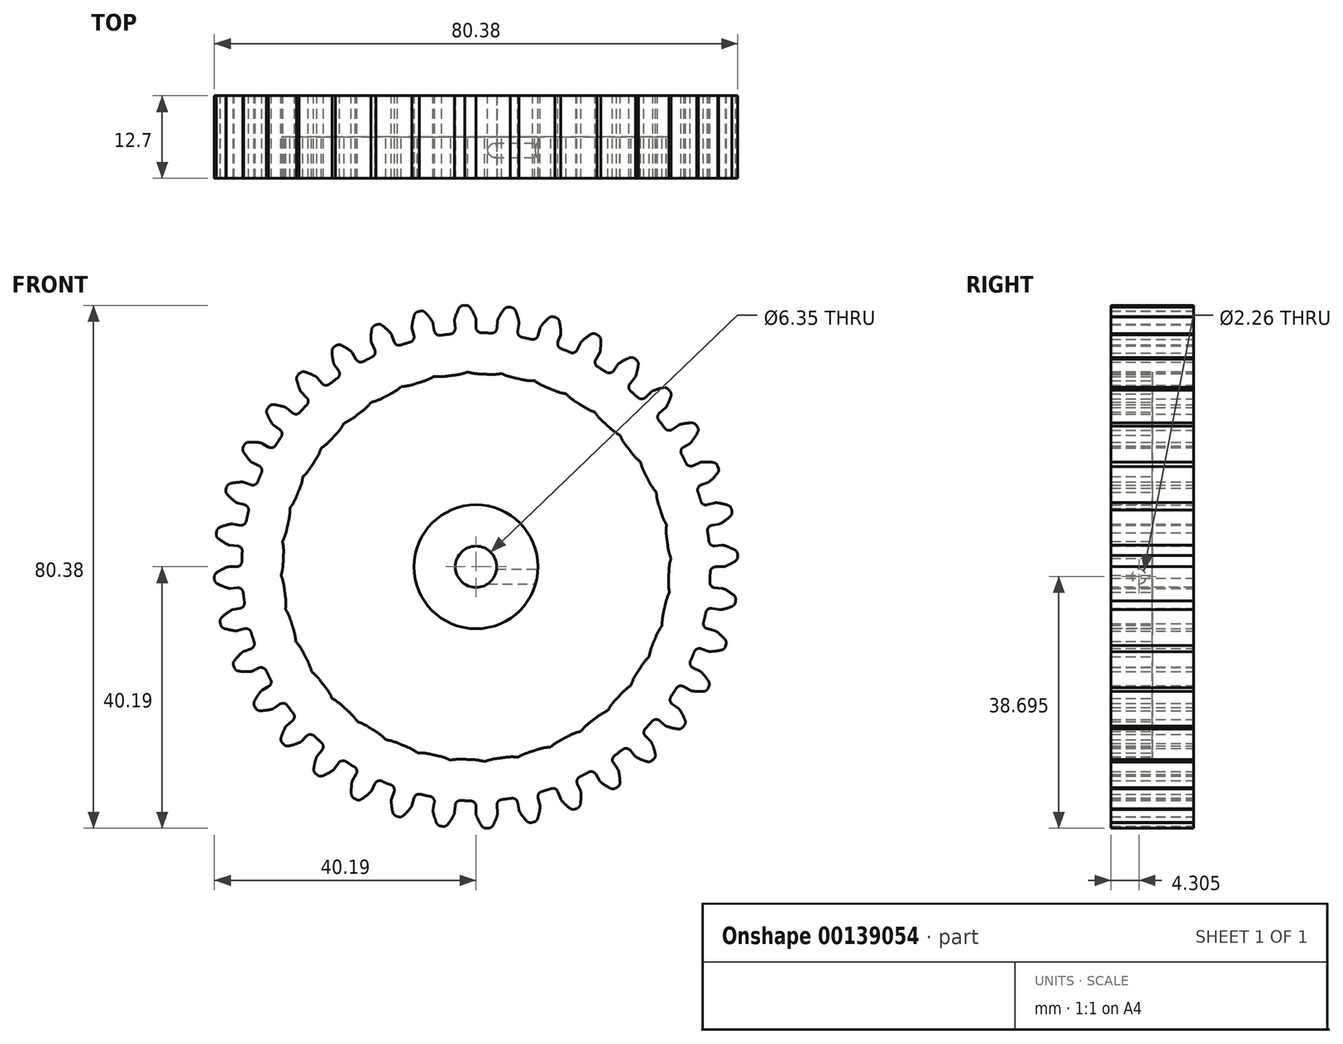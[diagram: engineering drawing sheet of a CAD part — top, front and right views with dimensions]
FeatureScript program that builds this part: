
annotation { "Feature Type Name" : "Feature", "Feature Type Description" : "" }
export const myFeature = defineFeature(function(context is Context, id is Id, definition is map)
    precondition{}
    {
        {
            var Q0;
            Q0=qCreatedBy(makeId("Front.planeOp"),FACE);
            var sketch = newSketch(context, id + "F0", { "sketchPlane" : qUnion([Q0])});
            skArc(sketch, "E0", {"start": v(-3.94, 35.77) * mm, "mid": v(-4.7, 35.68) * mm, "end": v(-5.45, 35.57) * mm});
            skArc(sketch, "E1", {"start": v(-0.06, 38.25) * mm, "mid": v(-0.43, 39.05) * mm, "end": v(-0.86, 39.8) * mm});
            skLineSegment(sketch, "E2", {"start": v(0, 37.94) * mm, "end": v(0, 36.8) * mm});
            skLineSegment(sketch, "E3", {"start": v(-1.58, 40.19) * mm, "end": v(-1.75, 40.18) * mm});
            skLineSegment(sketch, "E4.MirrorCS", {"start": v(-1.93, 40.17) * mm, "end": v(-1.75, 40.18) * mm});
            skArc(sketch, "E5.MirrorCS", {"start": v(-3.27, 38.11) * mm, "mid": v(-2.98, 38.94) * mm, "end": v(-2.61, 39.73) * mm});
            skLineSegment(sketch, "E6.MirrorCS", {"start": v(-3.3, 37.8) * mm, "end": v(-3.2, 36.66) * mm});
            skPoint(sketch, "E7.visualSharp", {"position": v(-3.32, 37.96) * mm});
            skArc(sketch, "E7.filletArc", {"start": v(-3.27, 38.11) * mm, "mid": v(-3.3, 37.96) * mm, "end": v(-3.3, 37.8) * mm});
            skPoint(sketch, "E8.visualSharp", {"position": v(0, 38.1) * mm});
            skArc(sketch, "E8.filletArc", {"start": v(0, 37.94) * mm, "mid": v(-0.02, 38.1) * mm, "end": v(-0.06, 38.25) * mm});
            skPoint(sketch, "E9.visualSharp", {"position": v(-2.38, 40.15) * mm});
            skArc(sketch, "E9.filletArc", {"start": v(-1.93, 40.17) * mm, "mid": v(-2.33, 40.04) * mm, "end": v(-2.61, 39.73) * mm});
            skPoint(sketch, "E10.visualSharp", {"position": v(-1.13, 40.2) * mm});
            skArc(sketch, "E10.filletArc", {"start": v(-0.86, 39.8) * mm, "mid": v(-1.17, 40.1) * mm, "end": v(-1.58, 40.19) * mm});
            skPoint(sketch, "E11.visualSharp", {"position": v(-3.14, 35.85) * mm});
            skArc(sketch, "E11.filletArc", {"start": v(-3.94, 35.77) * mm, "mid": v(-3.4, 36.06) * mm, "end": v(-3.2, 36.66) * mm});
            skPoint(sketch, "E12.visualSharp", {"position": v(0, 35.98) * mm});
            skArc(sketch, "E12.filletArc", {"start": v(0, 36.8) * mm, "mid": v(0.24, 36.22) * mm, "end": v(0.8, 35.97) * mm});
            skArc(sketch, "E13.1.0", {"start": v(-10.1, 34.54) * mm, "mid": v(-9.6, 34.93) * mm, "end": v(-9.52, 35.55) * mm});
            skLineSegment(sketch, "E13.1.1", {"start": v(-9.82, 36.65) * mm, "end": v(-9.52, 35.55) * mm});
            skArc(sketch, "E13.1.2", {"start": v(-9.84, 36.96) * mm, "mid": v(-9.85, 36.8) * mm, "end": v(-9.82, 36.65) * mm});
            skArc(sketch, "E13.1.3", {"start": v(-9.84, 36.96) * mm, "mid": v(-9.7, 37.83) * mm, "end": v(-9.47, 38.67) * mm});
            skArc(sketch, "E13.1.4", {"start": v(-8.87, 39.23) * mm, "mid": v(-9.25, 39.03) * mm, "end": v(-9.47, 38.67) * mm});
            skLineSegment(sketch, "E13.1.5", {"start": v(-8.87, 39.23) * mm, "end": v(-8.7, 39.27) * mm});
            skLineSegment(sketch, "E13.1.6", {"start": v(-8.54, 39.3) * mm, "end": v(-8.7, 39.27) * mm});
            skArc(sketch, "E13.1.7", {"start": v(-7.76, 39.05) * mm, "mid": v(-8.12, 39.28) * mm, "end": v(-8.54, 39.3) * mm});
            skArc(sketch, "E13.1.8", {"start": v(-6.7, 37.66) * mm, "mid": v(-7.2, 38.38) * mm, "end": v(-7.76, 39.05) * mm});
            skArc(sketch, "E13.1.9", {"start": v(-6.59, 37.37) * mm, "mid": v(-6.63, 37.52) * mm, "end": v(-6.7, 37.66) * mm});
            skArc(sketch, "E13.1.10", {"start": v(-6.4, 36.24) * mm, "mid": v(-6.06, 35.71) * mm, "end": v(-5.45, 35.57) * mm});
            skLineSegment(sketch, "E13.1.11", {"start": v(-6.59, 37.37) * mm, "end": v(-6.4, 36.24) * mm});
            skArc(sketch, "E13.2.0", {"start": v(-15.93, 32.26) * mm, "mid": v(-15.52, 32.73) * mm, "end": v(-15.55, 33.35) * mm});
            skLineSegment(sketch, "E13.2.1", {"start": v(-16.04, 34.39) * mm, "end": v(-15.55, 33.35) * mm});
            skArc(sketch, "E13.2.2", {"start": v(-16.11, 34.7) * mm, "mid": v(-16.09, 34.54) * mm, "end": v(-16.04, 34.39) * mm});
            skArc(sketch, "E13.2.3", {"start": v(-16.11, 34.7) * mm, "mid": v(-16.12, 35.57) * mm, "end": v(-16.04, 36.44) * mm});
            skArc(sketch, "E13.2.4", {"start": v(-15.55, 37.1) * mm, "mid": v(-15.88, 36.83) * mm, "end": v(-16.04, 36.44) * mm});
            skLineSegment(sketch, "E13.2.5", {"start": v(-15.55, 37.1) * mm, "end": v(-15.4, 37.16) * mm});
            skLineSegment(sketch, "E13.2.6", {"start": v(-15.23, 37.22) * mm, "end": v(-15.4, 37.16) * mm});
            skArc(sketch, "E13.2.7", {"start": v(-14.43, 37.11) * mm, "mid": v(-14.81, 37.27) * mm, "end": v(-15.23, 37.22) * mm});
            skArc(sketch, "E13.2.8", {"start": v(-13.14, 35.93) * mm, "mid": v(-13.76, 36.55) * mm, "end": v(-14.43, 37.11) * mm});
            skArc(sketch, "E13.2.9", {"start": v(-12.98, 35.65) * mm, "mid": v(-13.05, 35.8) * mm, "end": v(-13.14, 35.93) * mm});
            skArc(sketch, "E13.2.10", {"start": v(-12.59, 34.58) * mm, "mid": v(-12.17, 34.12) * mm, "end": v(-11.55, 34.08) * mm});
            skLineSegment(sketch, "E13.2.11", {"start": v(-12.98, 35.65) * mm, "end": v(-12.59, 34.58) * mm});
            skArc(sketch, "E13.3.0", {"start": v(-21.3, 29) * mm, "mid": v(-20.97, 29.54) * mm, "end": v(-21.1, 30.14) * mm});
            skLineSegment(sketch, "E13.3.1", {"start": v(-21.76, 31.08) * mm, "end": v(-21.1, 30.14) * mm});
            skArc(sketch, "E13.3.2", {"start": v(-21.9, 31.37) * mm, "mid": v(-21.84, 31.22) * mm, "end": v(-21.76, 31.08) * mm});
            skArc(sketch, "E13.3.3", {"start": v(-21.9, 31.37) * mm, "mid": v(-22.05, 32.23) * mm, "end": v(-22.13, 33.1) * mm});
            skArc(sketch, "E13.3.4", {"start": v(-21.76, 33.83) * mm, "mid": v(-22.04, 33.51) * mm, "end": v(-22.13, 33.1) * mm});
            skLineSegment(sketch, "E13.3.5", {"start": v(-21.76, 33.83) * mm, "end": v(-21.61, 33.92) * mm});
            skLineSegment(sketch, "E13.3.6", {"start": v(-21.46, 34.01) * mm, "end": v(-21.61, 33.92) * mm});
            skArc(sketch, "E13.3.7", {"start": v(-20.65, 34.04) * mm, "mid": v(-21.06, 34.14) * mm, "end": v(-21.46, 34.01) * mm});
            skArc(sketch, "E13.3.8", {"start": v(-19.18, 33.1) * mm, "mid": v(-19.9, 33.6) * mm, "end": v(-20.65, 34.04) * mm});
            skArc(sketch, "E13.3.9", {"start": v(-18.97, 32.86) * mm, "mid": v(-19.06, 32.99) * mm, "end": v(-19.18, 33.1) * mm});
            skArc(sketch, "E13.3.10", {"start": v(-18.4, 31.87) * mm, "mid": v(-17.9, 31.49) * mm, "end": v(-17.29, 31.56) * mm});
            skLineSegment(sketch, "E13.3.11", {"start": v(-18.97, 32.86) * mm, "end": v(-18.4, 31.87) * mm});
            skArc(sketch, "E13.4.0", {"start": v(-26, 24.87) * mm, "mid": v(-25.78, 25.45) * mm, "end": v(-26.02, 26.02) * mm});
            skLineSegment(sketch, "E13.4.1", {"start": v(-26.83, 26.83) * mm, "end": v(-26.02, 26.02) * mm});
            skArc(sketch, "E13.4.2", {"start": v(-27, 27.1) * mm, "mid": v(-26.93, 26.95) * mm, "end": v(-26.83, 26.83) * mm});
            skArc(sketch, "E13.4.3", {"start": v(-27, 27.1) * mm, "mid": v(-27.31, 27.91) * mm, "end": v(-27.54, 28.76) * mm});
            skArc(sketch, "E13.4.4", {"start": v(-27.3, 29.54) * mm, "mid": v(-27.52, 29.18) * mm, "end": v(-27.54, 28.76) * mm});
            skLineSegment(sketch, "E13.4.5", {"start": v(-27.3, 29.54) * mm, "end": v(-27.17, 29.65) * mm});
            skLineSegment(sketch, "E13.4.6", {"start": v(-27.04, 29.77) * mm, "end": v(-27.17, 29.65) * mm});
            skArc(sketch, "E13.4.7", {"start": v(-26.25, 29.94) * mm, "mid": v(-26.67, 29.96) * mm, "end": v(-27.04, 29.77) * mm});
            skArc(sketch, "E13.4.8", {"start": v(-24.63, 29.26) * mm, "mid": v(-25.43, 29.64) * mm, "end": v(-26.25, 29.94) * mm});
            skArc(sketch, "E13.4.9", {"start": v(-24.39, 29.07) * mm, "mid": v(-24.5, 29.18) * mm, "end": v(-24.63, 29.26) * mm});
            skArc(sketch, "E13.4.10", {"start": v(-23.65, 28.2) * mm, "mid": v(-23.1, 27.9) * mm, "end": v(-22.5, 28.08) * mm});
            skLineSegment(sketch, "E13.4.11", {"start": v(-24.39, 29.07) * mm, "end": v(-23.65, 28.2) * mm});
            skArc(sketch, "E13.5.0", {"start": v(-29.93, 19.97) * mm, "mid": v(-29.8, 20.58) * mm, "end": v(-30.14, 21.1) * mm});
            skLineSegment(sketch, "E13.5.1", {"start": v(-31.08, 21.76) * mm, "end": v(-30.14, 21.1) * mm});
            skArc(sketch, "E13.5.2", {"start": v(-31.3, 22) * mm, "mid": v(-31.2, 21.87) * mm, "end": v(-31.08, 21.76) * mm});
            skArc(sketch, "E13.5.3", {"start": v(-31.3, 22) * mm, "mid": v(-31.74, 22.75) * mm, "end": v(-32.11, 23.54) * mm});
            skArc(sketch, "E13.5.4", {"start": v(-32.01, 24.35) * mm, "mid": v(-32.17, 23.96) * mm, "end": v(-32.11, 23.54) * mm});
            skLineSegment(sketch, "E13.5.5", {"start": v(-32.01, 24.35) * mm, "end": v(-31.9, 24.49) * mm});
            skLineSegment(sketch, "E13.5.6", {"start": v(-31.8, 24.62) * mm, "end": v(-31.9, 24.49) * mm});
            skArc(sketch, "E13.5.7", {"start": v(-31.05, 24.93) * mm, "mid": v(-31.47, 24.87) * mm, "end": v(-31.8, 24.62) * mm});
            skArc(sketch, "E13.5.8", {"start": v(-29.34, 24.54) * mm, "mid": v(-30.19, 24.77) * mm, "end": v(-31.05, 24.93) * mm});
            skArc(sketch, "E13.5.9", {"start": v(-29.07, 24.39) * mm, "mid": v(-29.2, 24.48) * mm, "end": v(-29.34, 24.54) * mm});
            skArc(sketch, "E13.5.10", {"start": v(-28.2, 23.65) * mm, "mid": v(-27.6, 23.46) * mm, "end": v(-27.04, 23.74) * mm});
            skLineSegment(sketch, "E13.5.11", {"start": v(-29.07, 24.39) * mm, "end": v(-28.2, 23.65) * mm});
            skArc(sketch, "E13.6.0", {"start": v(-32.94, 14.47) * mm, "mid": v(-32.93, 15.1) * mm, "end": v(-33.35, 15.55) * mm});
            skLineSegment(sketch, "E13.6.1", {"start": v(-34.39, 16.04) * mm, "end": v(-33.35, 15.55) * mm});
            skArc(sketch, "E13.6.2", {"start": v(-34.64, 16.22) * mm, "mid": v(-34.52, 16.12) * mm, "end": v(-34.39, 16.04) * mm});
            skArc(sketch, "E13.6.3", {"start": v(-34.64, 16.22) * mm, "mid": v(-35.21, 16.89) * mm, "end": v(-35.71, 17.6) * mm});
            skArc(sketch, "E13.6.4", {"start": v(-35.75, 18.42) * mm, "mid": v(-35.84, 18) * mm, "end": v(-35.71, 17.6) * mm});
            skLineSegment(sketch, "E13.6.5", {"start": v(-35.75, 18.42) * mm, "end": v(-35.68, 18.57) * mm});
            skLineSegment(sketch, "E13.6.6", {"start": v(-35.6, 18.72) * mm, "end": v(-35.68, 18.57) * mm});
            skArc(sketch, "E13.6.7", {"start": v(-34.9, 19.16) * mm, "mid": v(-35.3, 19.03) * mm, "end": v(-35.6, 18.72) * mm});
            skArc(sketch, "E13.6.8", {"start": v(-33.16, 19.07) * mm, "mid": v(-34.03, 19.16) * mm, "end": v(-34.9, 19.16) * mm});
            skArc(sketch, "E13.6.9", {"start": v(-32.86, 18.97) * mm, "mid": v(-33, 19.04) * mm, "end": v(-33.16, 19.07) * mm});
            skArc(sketch, "E13.6.10", {"start": v(-31.87, 18.4) * mm, "mid": v(-31.25, 18.31) * mm, "end": v(-30.75, 18.69) * mm});
            skLineSegment(sketch, "E13.6.11", {"start": v(-32.86, 18.97) * mm, "end": v(-31.87, 18.4) * mm});
            skArc(sketch, "E13.7.0", {"start": v(-34.96, 8.53) * mm, "mid": v(-35.05, 9.15) * mm, "end": v(-35.55, 9.52) * mm});
            skLineSegment(sketch, "E13.7.1", {"start": v(-36.65, 9.82) * mm, "end": v(-35.55, 9.52) * mm});
            skArc(sketch, "E13.7.2", {"start": v(-36.93, 9.96) * mm, "mid": v(-36.8, 9.88) * mm, "end": v(-36.65, 9.82) * mm});
            skArc(sketch, "E13.7.3", {"start": v(-36.93, 9.96) * mm, "mid": v(-37.6, 10.52) * mm, "end": v(-38.23, 11.14) * mm});
            skArc(sketch, "E13.7.4", {"start": v(-38.4, 11.93) * mm, "mid": v(-38.42, 11.5) * mm, "end": v(-38.23, 11.14) * mm});
            skLineSegment(sketch, "E13.7.5", {"start": v(-38.4, 11.93) * mm, "end": v(-38.36, 12.1) * mm});
            skLineSegment(sketch, "E13.7.6", {"start": v(-38.3, 12.26) * mm, "end": v(-38.36, 12.1) * mm});
            skArc(sketch, "E13.7.7", {"start": v(-37.7, 12.8) * mm, "mid": v(-38.08, 12.61) * mm, "end": v(-38.3, 12.26) * mm});
            skArc(sketch, "E13.7.8", {"start": v(-35.97, 13.03) * mm, "mid": v(-36.84, 12.96) * mm, "end": v(-37.7, 12.8) * mm});
            skArc(sketch, "E13.7.9", {"start": v(-35.65, 12.98) * mm, "mid": v(-35.8, 13.02) * mm, "end": v(-35.97, 13.03) * mm});
            skArc(sketch, "E13.7.10", {"start": v(-34.58, 12.59) * mm, "mid": v(-33.96, 12.6) * mm, "end": v(-33.53, 13.06) * mm});
            skLineSegment(sketch, "E13.7.11", {"start": v(-35.65, 12.98) * mm, "end": v(-34.58, 12.59) * mm});
            skArc(sketch, "E13.8.0", {"start": v(-35.9, 2.33) * mm, "mid": v(-36.1, 2.92) * mm, "end": v(-36.66, 3.2) * mm});
            skLineSegment(sketch, "E13.8.1", {"start": v(-37.8, 3.3) * mm, "end": v(-36.66, 3.2) * mm});
            skArc(sketch, "E13.8.2", {"start": v(-38.1, 3.4) * mm, "mid": v(-37.95, 3.34) * mm, "end": v(-37.8, 3.3) * mm});
            skArc(sketch, "E13.8.3", {"start": v(-38.1, 3.4) * mm, "mid": v(-38.86, 3.83) * mm, "end": v(-39.58, 4.33) * mm});
            skArc(sketch, "E13.8.4", {"start": v(-39.9, 5.08) * mm, "mid": v(-39.84, 4.66) * mm, "end": v(-39.58, 4.33) * mm});
            skLineSegment(sketch, "E13.8.5", {"start": v(-39.9, 5.08) * mm, "end": v(-39.88, 5.25) * mm});
            skLineSegment(sketch, "E13.8.6", {"start": v(-39.85, 5.42) * mm, "end": v(-39.88, 5.25) * mm});
            skArc(sketch, "E13.8.7", {"start": v(-39.35, 6.06) * mm, "mid": v(-39.69, 5.8) * mm, "end": v(-39.85, 5.42) * mm});
            skArc(sketch, "E13.8.8", {"start": v(-37.68, 6.58) * mm, "mid": v(-38.53, 6.36) * mm, "end": v(-39.35, 6.06) * mm});
            skArc(sketch, "E13.8.9", {"start": v(-37.37, 6.59) * mm, "mid": v(-37.52, 6.6) * mm, "end": v(-37.68, 6.58) * mm});
            skArc(sketch, "E13.8.10", {"start": v(-36.24, 6.4) * mm, "mid": v(-35.63, 6.52) * mm, "end": v(-35.29, 7.04) * mm});
            skLineSegment(sketch, "E13.8.11", {"start": v(-37.37, 6.59) * mm, "end": v(-36.24, 6.4) * mm});
            skArc(sketch, "E13.9.0", {"start": v(-35.77, -3.94) * mm, "mid": v(-36.06, -3.4) * mm, "end": v(-36.66, -3.2) * mm});
            skLineSegment(sketch, "E13.9.1", {"start": v(-37.8, -3.3) * mm, "end": v(-36.66, -3.2) * mm});
            skArc(sketch, "E13.9.2", {"start": v(-38.11, -3.27) * mm, "mid": v(-37.96, -3.3) * mm, "end": v(-37.8, -3.3) * mm});
            skArc(sketch, "E13.9.3", {"start": v(-38.11, -3.27) * mm, "mid": v(-38.94, -2.98) * mm, "end": v(-39.73, -2.61) * mm});
            skArc(sketch, "E13.9.4", {"start": v(-40.17, -1.93) * mm, "mid": v(-40.04, -2.33) * mm, "end": v(-39.73, -2.61) * mm});
            skLineSegment(sketch, "E13.9.5", {"start": v(-40.17, -1.93) * mm, "end": v(-40.18, -1.75) * mm});
            skLineSegment(sketch, "E13.9.6", {"start": v(-40.19, -1.58) * mm, "end": v(-40.18, -1.75) * mm});
            skArc(sketch, "E13.9.7", {"start": v(-39.8, -0.86) * mm, "mid": v(-40.1, -1.17) * mm, "end": v(-40.19, -1.58) * mm});
            skArc(sketch, "E13.9.8", {"start": v(-38.25, -0.06) * mm, "mid": v(-39.05, -0.43) * mm, "end": v(-39.8, -0.86) * mm});
            skArc(sketch, "E13.9.9", {"start": v(-37.94, 0) * mm, "mid": v(-38.1, -0.02) * mm, "end": v(-38.25, -0.06) * mm});
            skArc(sketch, "E13.9.10", {"start": v(-36.8, 0) * mm, "mid": v(-36.22, 0.24) * mm, "end": v(-35.97, 0.8) * mm});
            skLineSegment(sketch, "E13.9.11", {"start": v(-37.94, 0) * mm, "end": v(-36.8, 0) * mm});
            skArc(sketch, "E13.10.0", {"start": v(-34.54, -10.1) * mm, "mid": v(-34.93, -9.6) * mm, "end": v(-35.55, -9.52) * mm});
            skLineSegment(sketch, "E13.10.1", {"start": v(-36.65, -9.82) * mm, "end": v(-35.55, -9.52) * mm});
            skArc(sketch, "E13.10.2", {"start": v(-36.96, -9.84) * mm, "mid": v(-36.8, -9.85) * mm, "end": v(-36.65, -9.82) * mm});
            skArc(sketch, "E13.10.3", {"start": v(-36.96, -9.84) * mm, "mid": v(-37.83, -9.7) * mm, "end": v(-38.67, -9.47) * mm});
            skArc(sketch, "E13.10.4", {"start": v(-39.23, -8.87) * mm, "mid": v(-39.03, -9.25) * mm, "end": v(-38.67, -9.47) * mm});
            skLineSegment(sketch, "E13.10.5", {"start": v(-39.23, -8.87) * mm, "end": v(-39.27, -8.7) * mm});
            skLineSegment(sketch, "E13.10.6", {"start": v(-39.3, -8.54) * mm, "end": v(-39.27, -8.7) * mm});
            skArc(sketch, "E13.10.7", {"start": v(-39.05, -7.76) * mm, "mid": v(-39.28, -8.12) * mm, "end": v(-39.3, -8.54) * mm});
            skArc(sketch, "E13.10.8", {"start": v(-37.66, -6.7) * mm, "mid": v(-38.38, -7.2) * mm, "end": v(-39.05, -7.76) * mm});
            skArc(sketch, "E13.10.9", {"start": v(-37.37, -6.59) * mm, "mid": v(-37.52, -6.63) * mm, "end": v(-37.66, -6.7) * mm});
            skArc(sketch, "E13.10.10", {"start": v(-36.24, -6.4) * mm, "mid": v(-35.71, -6.06) * mm, "end": v(-35.57, -5.45) * mm});
            skLineSegment(sketch, "E13.10.11", {"start": v(-37.37, -6.59) * mm, "end": v(-36.24, -6.4) * mm});
            skArc(sketch, "E13.11.0", {"start": v(-32.26, -15.93) * mm, "mid": v(-32.73, -15.52) * mm, "end": v(-33.35, -15.55) * mm});
            skLineSegment(sketch, "E13.11.1", {"start": v(-34.39, -16.04) * mm, "end": v(-33.35, -15.55) * mm});
            skArc(sketch, "E13.11.2", {"start": v(-34.7, -16.11) * mm, "mid": v(-34.54, -16.09) * mm, "end": v(-34.39, -16.04) * mm});
            skArc(sketch, "E13.11.3", {"start": v(-34.7, -16.11) * mm, "mid": v(-35.57, -16.12) * mm, "end": v(-36.44, -16.04) * mm});
            skArc(sketch, "E13.11.4", {"start": v(-37.1, -15.55) * mm, "mid": v(-36.83, -15.88) * mm, "end": v(-36.44, -16.04) * mm});
            skLineSegment(sketch, "E13.11.5", {"start": v(-37.1, -15.55) * mm, "end": v(-37.16, -15.4) * mm});
            skLineSegment(sketch, "E13.11.6", {"start": v(-37.22, -15.23) * mm, "end": v(-37.16, -15.4) * mm});
            skArc(sketch, "E13.11.7", {"start": v(-37.11, -14.43) * mm, "mid": v(-37.27, -14.81) * mm, "end": v(-37.22, -15.23) * mm});
            skArc(sketch, "E13.11.8", {"start": v(-35.93, -13.14) * mm, "mid": v(-36.55, -13.76) * mm, "end": v(-37.11, -14.43) * mm});
            skArc(sketch, "E13.11.9", {"start": v(-35.65, -12.98) * mm, "mid": v(-35.8, -13.05) * mm, "end": v(-35.93, -13.14) * mm});
            skArc(sketch, "E13.11.10", {"start": v(-34.58, -12.59) * mm, "mid": v(-34.12, -12.17) * mm, "end": v(-34.08, -11.55) * mm});
            skLineSegment(sketch, "E13.11.11", {"start": v(-35.65, -12.98) * mm, "end": v(-34.58, -12.59) * mm});
            skArc(sketch, "E13.12.0", {"start": v(-29, -21.3) * mm, "mid": v(-29.54, -20.97) * mm, "end": v(-30.14, -21.1) * mm});
            skLineSegment(sketch, "E13.12.1", {"start": v(-31.08, -21.76) * mm, "end": v(-30.14, -21.1) * mm});
            skArc(sketch, "E13.12.2", {"start": v(-31.37, -21.9) * mm, "mid": v(-31.22, -21.84) * mm, "end": v(-31.08, -21.76) * mm});
            skArc(sketch, "E13.12.3", {"start": v(-31.37, -21.9) * mm, "mid": v(-32.23, -22.05) * mm, "end": v(-33.1, -22.13) * mm});
            skArc(sketch, "E13.12.4", {"start": v(-33.83, -21.76) * mm, "mid": v(-33.51, -22.04) * mm, "end": v(-33.1, -22.13) * mm});
            skLineSegment(sketch, "E13.12.5", {"start": v(-33.83, -21.76) * mm, "end": v(-33.92, -21.61) * mm});
            skLineSegment(sketch, "E13.12.6", {"start": v(-34.01, -21.46) * mm, "end": v(-33.92, -21.61) * mm});
            skArc(sketch, "E13.12.7", {"start": v(-34.04, -20.65) * mm, "mid": v(-34.14, -21.06) * mm, "end": v(-34.01, -21.46) * mm});
            skArc(sketch, "E13.12.8", {"start": v(-33.1, -19.18) * mm, "mid": v(-33.6, -19.9) * mm, "end": v(-34.04, -20.65) * mm});
            skArc(sketch, "E13.12.9", {"start": v(-32.86, -18.97) * mm, "mid": v(-32.99, -19.06) * mm, "end": v(-33.1, -19.18) * mm});
            skArc(sketch, "E13.12.10", {"start": v(-31.87, -18.4) * mm, "mid": v(-31.49, -17.9) * mm, "end": v(-31.56, -17.29) * mm});
            skLineSegment(sketch, "E13.12.11", {"start": v(-32.86, -18.97) * mm, "end": v(-31.87, -18.4) * mm});
            skArc(sketch, "E13.13.0", {"start": v(-24.87, -26) * mm, "mid": v(-25.45, -25.78) * mm, "end": v(-26.02, -26.02) * mm});
            skLineSegment(sketch, "E13.13.1", {"start": v(-26.83, -26.83) * mm, "end": v(-26.02, -26.02) * mm});
            skArc(sketch, "E13.13.2", {"start": v(-27.1, -27) * mm, "mid": v(-26.95, -26.93) * mm, "end": v(-26.83, -26.83) * mm});
            skArc(sketch, "E13.13.3", {"start": v(-27.1, -27) * mm, "mid": v(-27.91, -27.31) * mm, "end": v(-28.76, -27.54) * mm});
            skArc(sketch, "E13.13.4", {"start": v(-29.54, -27.3) * mm, "mid": v(-29.18, -27.52) * mm, "end": v(-28.76, -27.54) * mm});
            skLineSegment(sketch, "E13.13.5", {"start": v(-29.54, -27.3) * mm, "end": v(-29.65, -27.17) * mm});
            skLineSegment(sketch, "E13.13.6", {"start": v(-29.77, -27.04) * mm, "end": v(-29.65, -27.17) * mm});
            skArc(sketch, "E13.13.7", {"start": v(-29.94, -26.25) * mm, "mid": v(-29.96, -26.67) * mm, "end": v(-29.77, -27.04) * mm});
            skArc(sketch, "E13.13.8", {"start": v(-29.26, -24.63) * mm, "mid": v(-29.64, -25.43) * mm, "end": v(-29.94, -26.25) * mm});
            skArc(sketch, "E13.13.9", {"start": v(-29.07, -24.39) * mm, "mid": v(-29.18, -24.5) * mm, "end": v(-29.26, -24.63) * mm});
            skArc(sketch, "E13.13.10", {"start": v(-28.2, -23.65) * mm, "mid": v(-27.9, -23.1) * mm, "end": v(-28.08, -22.5) * mm});
            skLineSegment(sketch, "E13.13.11", {"start": v(-29.07, -24.39) * mm, "end": v(-28.2, -23.65) * mm});
            skArc(sketch, "E13.14.0", {"start": v(-19.97, -29.93) * mm, "mid": v(-20.58, -29.8) * mm, "end": v(-21.1, -30.14) * mm});
            skLineSegment(sketch, "E13.14.1", {"start": v(-21.76, -31.08) * mm, "end": v(-21.1, -30.14) * mm});
            skArc(sketch, "E13.14.2", {"start": v(-22, -31.3) * mm, "mid": v(-21.87, -31.2) * mm, "end": v(-21.76, -31.08) * mm});
            skArc(sketch, "E13.14.3", {"start": v(-22, -31.3) * mm, "mid": v(-22.75, -31.74) * mm, "end": v(-23.54, -32.11) * mm});
            skArc(sketch, "E13.14.4", {"start": v(-24.35, -32.01) * mm, "mid": v(-23.96, -32.17) * mm, "end": v(-23.54, -32.11) * mm});
            skLineSegment(sketch, "E13.14.5", {"start": v(-24.35, -32.01) * mm, "end": v(-24.49, -31.9) * mm});
            skLineSegment(sketch, "E13.14.6", {"start": v(-24.62, -31.8) * mm, "end": v(-24.49, -31.9) * mm});
            skArc(sketch, "E13.14.7", {"start": v(-24.93, -31.05) * mm, "mid": v(-24.87, -31.47) * mm, "end": v(-24.62, -31.8) * mm});
            skArc(sketch, "E13.14.8", {"start": v(-24.54, -29.34) * mm, "mid": v(-24.77, -30.19) * mm, "end": v(-24.93, -31.05) * mm});
            skArc(sketch, "E13.14.9", {"start": v(-24.39, -29.07) * mm, "mid": v(-24.48, -29.2) * mm, "end": v(-24.54, -29.34) * mm});
            skArc(sketch, "E13.14.10", {"start": v(-23.65, -28.2) * mm, "mid": v(-23.46, -27.6) * mm, "end": v(-23.74, -27.04) * mm});
            skLineSegment(sketch, "E13.14.11", {"start": v(-24.39, -29.07) * mm, "end": v(-23.65, -28.2) * mm});
            skArc(sketch, "E13.15.0", {"start": v(-14.47, -32.94) * mm, "mid": v(-15.1, -32.93) * mm, "end": v(-15.55, -33.35) * mm});
            skLineSegment(sketch, "E13.15.1", {"start": v(-16.04, -34.39) * mm, "end": v(-15.55, -33.35) * mm});
            skArc(sketch, "E13.15.2", {"start": v(-16.22, -34.64) * mm, "mid": v(-16.12, -34.52) * mm, "end": v(-16.04, -34.39) * mm});
            skArc(sketch, "E13.15.3", {"start": v(-16.22, -34.64) * mm, "mid": v(-16.89, -35.21) * mm, "end": v(-17.6, -35.71) * mm});
            skArc(sketch, "E13.15.4", {"start": v(-18.42, -35.75) * mm, "mid": v(-18, -35.84) * mm, "end": v(-17.6, -35.71) * mm});
            skLineSegment(sketch, "E13.15.5", {"start": v(-18.42, -35.75) * mm, "end": v(-18.57, -35.68) * mm});
            skLineSegment(sketch, "E13.15.6", {"start": v(-18.72, -35.6) * mm, "end": v(-18.57, -35.68) * mm});
            skArc(sketch, "E13.15.7", {"start": v(-19.16, -34.9) * mm, "mid": v(-19.03, -35.3) * mm, "end": v(-18.72, -35.6) * mm});
            skArc(sketch, "E13.15.8", {"start": v(-19.07, -33.16) * mm, "mid": v(-19.16, -34.03) * mm, "end": v(-19.16, -34.9) * mm});
            skArc(sketch, "E13.15.9", {"start": v(-18.97, -32.86) * mm, "mid": v(-19.04, -33) * mm, "end": v(-19.07, -33.16) * mm});
            skArc(sketch, "E13.15.10", {"start": v(-18.4, -31.87) * mm, "mid": v(-18.31, -31.25) * mm, "end": v(-18.69, -30.75) * mm});
            skLineSegment(sketch, "E13.15.11", {"start": v(-18.97, -32.86) * mm, "end": v(-18.4, -31.87) * mm});
            skArc(sketch, "E13.16.0", {"start": v(-8.53, -34.96) * mm, "mid": v(-9.15, -35.05) * mm, "end": v(-9.52, -35.55) * mm});
            skLineSegment(sketch, "E13.16.1", {"start": v(-9.82, -36.65) * mm, "end": v(-9.52, -35.55) * mm});
            skArc(sketch, "E13.16.2", {"start": v(-9.96, -36.93) * mm, "mid": v(-9.88, -36.8) * mm, "end": v(-9.82, -36.65) * mm});
            skArc(sketch, "E13.16.3", {"start": v(-9.96, -36.93) * mm, "mid": v(-10.52, -37.6) * mm, "end": v(-11.14, -38.23) * mm});
            skArc(sketch, "E13.16.4", {"start": v(-11.93, -38.4) * mm, "mid": v(-11.5, -38.42) * mm, "end": v(-11.14, -38.23) * mm});
            skLineSegment(sketch, "E13.16.5", {"start": v(-11.93, -38.4) * mm, "end": v(-12.1, -38.36) * mm});
            skLineSegment(sketch, "E13.16.6", {"start": v(-12.26, -38.3) * mm, "end": v(-12.1, -38.36) * mm});
            skArc(sketch, "E13.16.7", {"start": v(-12.8, -37.7) * mm, "mid": v(-12.61, -38.08) * mm, "end": v(-12.26, -38.3) * mm});
            skArc(sketch, "E13.16.8", {"start": v(-13.03, -35.97) * mm, "mid": v(-12.96, -36.84) * mm, "end": v(-12.8, -37.7) * mm});
            skArc(sketch, "E13.16.9", {"start": v(-12.98, -35.65) * mm, "mid": v(-13.02, -35.8) * mm, "end": v(-13.03, -35.97) * mm});
            skArc(sketch, "E13.16.10", {"start": v(-12.59, -34.58) * mm, "mid": v(-12.6, -33.96) * mm, "end": v(-13.06, -33.53) * mm});
            skLineSegment(sketch, "E13.16.11", {"start": v(-12.98, -35.65) * mm, "end": v(-12.59, -34.58) * mm});
            skArc(sketch, "E13.17.0", {"start": v(-2.33, -35.9) * mm, "mid": v(-2.92, -36.1) * mm, "end": v(-3.2, -36.66) * mm});
            skLineSegment(sketch, "E13.17.1", {"start": v(-3.3, -37.8) * mm, "end": v(-3.2, -36.66) * mm});
            skArc(sketch, "E13.17.2", {"start": v(-3.4, -38.1) * mm, "mid": v(-3.34, -37.95) * mm, "end": v(-3.3, -37.8) * mm});
            skArc(sketch, "E13.17.3", {"start": v(-3.4, -38.1) * mm, "mid": v(-3.83, -38.86) * mm, "end": v(-4.33, -39.58) * mm});
            skArc(sketch, "E13.17.4", {"start": v(-5.08, -39.9) * mm, "mid": v(-4.66, -39.84) * mm, "end": v(-4.33, -39.58) * mm});
            skLineSegment(sketch, "E13.17.5", {"start": v(-5.08, -39.9) * mm, "end": v(-5.25, -39.88) * mm});
            skLineSegment(sketch, "E13.17.6", {"start": v(-5.42, -39.85) * mm, "end": v(-5.25, -39.88) * mm});
            skArc(sketch, "E13.17.7", {"start": v(-6.06, -39.35) * mm, "mid": v(-5.8, -39.69) * mm, "end": v(-5.42, -39.85) * mm});
            skArc(sketch, "E13.17.8", {"start": v(-6.58, -37.68) * mm, "mid": v(-6.36, -38.53) * mm, "end": v(-6.06, -39.35) * mm});
            skArc(sketch, "E13.17.9", {"start": v(-6.59, -37.37) * mm, "mid": v(-6.6, -37.52) * mm, "end": v(-6.58, -37.68) * mm});
            skArc(sketch, "E13.17.10", {"start": v(-6.4, -36.24) * mm, "mid": v(-6.52, -35.63) * mm, "end": v(-7.04, -35.29) * mm});
            skLineSegment(sketch, "E13.17.11", {"start": v(-6.59, -37.37) * mm, "end": v(-6.4, -36.24) * mm});
            skArc(sketch, "E13.18.0", {"start": v(3.94, -35.77) * mm, "mid": v(3.4, -36.06) * mm, "end": v(3.2, -36.66) * mm});
            skLineSegment(sketch, "E13.18.1", {"start": v(3.3, -37.8) * mm, "end": v(3.2, -36.66) * mm});
            skArc(sketch, "E13.18.2", {"start": v(3.27, -38.11) * mm, "mid": v(3.3, -37.96) * mm, "end": v(3.3, -37.8) * mm});
            skArc(sketch, "E13.18.3", {"start": v(3.27, -38.11) * mm, "mid": v(2.98, -38.94) * mm, "end": v(2.61, -39.73) * mm});
            skArc(sketch, "E13.18.4", {"start": v(1.93, -40.17) * mm, "mid": v(2.33, -40.04) * mm, "end": v(2.61, -39.73) * mm});
            skLineSegment(sketch, "E13.18.5", {"start": v(1.93, -40.17) * mm, "end": v(1.75, -40.18) * mm});
            skLineSegment(sketch, "E13.18.6", {"start": v(1.58, -40.19) * mm, "end": v(1.75, -40.18) * mm});
            skArc(sketch, "E13.18.7", {"start": v(0.86, -39.8) * mm, "mid": v(1.17, -40.1) * mm, "end": v(1.58, -40.19) * mm});
            skArc(sketch, "E13.18.8", {"start": v(0.06, -38.25) * mm, "mid": v(0.43, -39.05) * mm, "end": v(0.86, -39.8) * mm});
            skArc(sketch, "E13.18.9", {"start": v(0, -37.94) * mm, "mid": v(0.02, -38.1) * mm, "end": v(0.06, -38.25) * mm});
            skArc(sketch, "E13.18.10", {"start": v(0, -36.8) * mm, "mid": v(-0.24, -36.22) * mm, "end": v(-0.8, -35.97) * mm});
            skLineSegment(sketch, "E13.18.11", {"start": v(0, -37.94) * mm, "end": v(0, -36.8) * mm});
            skArc(sketch, "E13.19.0", {"start": v(10.1, -34.54) * mm, "mid": v(9.6, -34.93) * mm, "end": v(9.52, -35.55) * mm});
            skLineSegment(sketch, "E13.19.1", {"start": v(9.82, -36.65) * mm, "end": v(9.52, -35.55) * mm});
            skArc(sketch, "E13.19.2", {"start": v(9.84, -36.96) * mm, "mid": v(9.85, -36.8) * mm, "end": v(9.82, -36.65) * mm});
            skArc(sketch, "E13.19.3", {"start": v(9.84, -36.96) * mm, "mid": v(9.7, -37.83) * mm, "end": v(9.47, -38.67) * mm});
            skArc(sketch, "E13.19.4", {"start": v(8.87, -39.23) * mm, "mid": v(9.25, -39.03) * mm, "end": v(9.47, -38.67) * mm});
            skLineSegment(sketch, "E13.19.5", {"start": v(8.87, -39.23) * mm, "end": v(8.7, -39.27) * mm});
            skLineSegment(sketch, "E13.19.6", {"start": v(8.54, -39.3) * mm, "end": v(8.7, -39.27) * mm});
            skArc(sketch, "E13.19.7", {"start": v(7.76, -39.05) * mm, "mid": v(8.12, -39.28) * mm, "end": v(8.54, -39.3) * mm});
            skArc(sketch, "E13.19.8", {"start": v(6.7, -37.66) * mm, "mid": v(7.2, -38.38) * mm, "end": v(7.76, -39.05) * mm});
            skArc(sketch, "E13.19.9", {"start": v(6.59, -37.37) * mm, "mid": v(6.63, -37.52) * mm, "end": v(6.7, -37.66) * mm});
            skArc(sketch, "E13.19.10", {"start": v(6.4, -36.24) * mm, "mid": v(6.06, -35.71) * mm, "end": v(5.45, -35.57) * mm});
            skLineSegment(sketch, "E13.19.11", {"start": v(6.59, -37.37) * mm, "end": v(6.4, -36.24) * mm});
            skArc(sketch, "E13.20.0", {"start": v(15.93, -32.26) * mm, "mid": v(15.52, -32.73) * mm, "end": v(15.55, -33.35) * mm});
            skLineSegment(sketch, "E13.20.1", {"start": v(16.04, -34.39) * mm, "end": v(15.55, -33.35) * mm});
            skArc(sketch, "E13.20.2", {"start": v(16.11, -34.7) * mm, "mid": v(16.09, -34.54) * mm, "end": v(16.04, -34.39) * mm});
            skArc(sketch, "E13.20.3", {"start": v(16.11, -34.7) * mm, "mid": v(16.12, -35.57) * mm, "end": v(16.04, -36.44) * mm});
            skArc(sketch, "E13.20.4", {"start": v(15.55, -37.1) * mm, "mid": v(15.88, -36.83) * mm, "end": v(16.04, -36.44) * mm});
            skLineSegment(sketch, "E13.20.5", {"start": v(15.55, -37.1) * mm, "end": v(15.4, -37.16) * mm});
            skLineSegment(sketch, "E13.20.6", {"start": v(15.23, -37.22) * mm, "end": v(15.4, -37.16) * mm});
            skArc(sketch, "E13.20.7", {"start": v(14.43, -37.11) * mm, "mid": v(14.81, -37.27) * mm, "end": v(15.23, -37.22) * mm});
            skArc(sketch, "E13.20.8", {"start": v(13.14, -35.93) * mm, "mid": v(13.76, -36.55) * mm, "end": v(14.43, -37.11) * mm});
            skArc(sketch, "E13.20.9", {"start": v(12.98, -35.65) * mm, "mid": v(13.05, -35.8) * mm, "end": v(13.14, -35.93) * mm});
            skArc(sketch, "E13.20.10", {"start": v(12.59, -34.58) * mm, "mid": v(12.17, -34.12) * mm, "end": v(11.55, -34.08) * mm});
            skLineSegment(sketch, "E13.20.11", {"start": v(12.98, -35.65) * mm, "end": v(12.59, -34.58) * mm});
            skArc(sketch, "E13.21.0", {"start": v(21.3, -29) * mm, "mid": v(20.97, -29.54) * mm, "end": v(21.1, -30.14) * mm});
            skLineSegment(sketch, "E13.21.1", {"start": v(21.76, -31.08) * mm, "end": v(21.1, -30.14) * mm});
            skArc(sketch, "E13.21.2", {"start": v(21.9, -31.37) * mm, "mid": v(21.84, -31.22) * mm, "end": v(21.76, -31.08) * mm});
            skArc(sketch, "E13.21.3", {"start": v(21.9, -31.37) * mm, "mid": v(22.05, -32.23) * mm, "end": v(22.13, -33.1) * mm});
            skArc(sketch, "E13.21.4", {"start": v(21.76, -33.83) * mm, "mid": v(22.04, -33.51) * mm, "end": v(22.13, -33.1) * mm});
            skLineSegment(sketch, "E13.21.5", {"start": v(21.76, -33.83) * mm, "end": v(21.61, -33.92) * mm});
            skLineSegment(sketch, "E13.21.6", {"start": v(21.46, -34.01) * mm, "end": v(21.61, -33.92) * mm});
            skArc(sketch, "E13.21.7", {"start": v(20.65, -34.04) * mm, "mid": v(21.06, -34.14) * mm, "end": v(21.46, -34.01) * mm});
            skArc(sketch, "E13.21.8", {"start": v(19.18, -33.1) * mm, "mid": v(19.9, -33.6) * mm, "end": v(20.65, -34.04) * mm});
            skArc(sketch, "E13.21.9", {"start": v(18.97, -32.86) * mm, "mid": v(19.06, -32.99) * mm, "end": v(19.18, -33.1) * mm});
            skArc(sketch, "E13.21.10", {"start": v(18.4, -31.87) * mm, "mid": v(17.9, -31.49) * mm, "end": v(17.29, -31.56) * mm});
            skLineSegment(sketch, "E13.21.11", {"start": v(18.97, -32.86) * mm, "end": v(18.4, -31.87) * mm});
            skArc(sketch, "E13.22.0", {"start": v(26, -24.87) * mm, "mid": v(25.78, -25.45) * mm, "end": v(26.02, -26.02) * mm});
            skLineSegment(sketch, "E13.22.1", {"start": v(26.83, -26.83) * mm, "end": v(26.02, -26.02) * mm});
            skArc(sketch, "E13.22.2", {"start": v(27, -27.1) * mm, "mid": v(26.93, -26.95) * mm, "end": v(26.83, -26.83) * mm});
            skArc(sketch, "E13.22.3", {"start": v(27, -27.1) * mm, "mid": v(27.31, -27.91) * mm, "end": v(27.54, -28.76) * mm});
            skArc(sketch, "E13.22.4", {"start": v(27.3, -29.54) * mm, "mid": v(27.52, -29.18) * mm, "end": v(27.54, -28.76) * mm});
            skLineSegment(sketch, "E13.22.5", {"start": v(27.3, -29.54) * mm, "end": v(27.17, -29.65) * mm});
            skLineSegment(sketch, "E13.22.6", {"start": v(27.04, -29.77) * mm, "end": v(27.17, -29.65) * mm});
            skArc(sketch, "E13.22.7", {"start": v(26.25, -29.94) * mm, "mid": v(26.67, -29.96) * mm, "end": v(27.04, -29.77) * mm});
            skArc(sketch, "E13.22.8", {"start": v(24.63, -29.26) * mm, "mid": v(25.43, -29.64) * mm, "end": v(26.25, -29.94) * mm});
            skArc(sketch, "E13.22.9", {"start": v(24.39, -29.07) * mm, "mid": v(24.5, -29.18) * mm, "end": v(24.63, -29.26) * mm});
            skArc(sketch, "E13.22.10", {"start": v(23.65, -28.2) * mm, "mid": v(23.1, -27.9) * mm, "end": v(22.5, -28.08) * mm});
            skLineSegment(sketch, "E13.22.11", {"start": v(24.39, -29.07) * mm, "end": v(23.65, -28.2) * mm});
            skArc(sketch, "E13.23.0", {"start": v(29.93, -19.97) * mm, "mid": v(29.8, -20.58) * mm, "end": v(30.14, -21.1) * mm});
            skLineSegment(sketch, "E13.23.1", {"start": v(31.08, -21.76) * mm, "end": v(30.14, -21.1) * mm});
            skArc(sketch, "E13.23.2", {"start": v(31.3, -22) * mm, "mid": v(31.2, -21.87) * mm, "end": v(31.08, -21.76) * mm});
            skArc(sketch, "E13.23.3", {"start": v(31.3, -22) * mm, "mid": v(31.74, -22.75) * mm, "end": v(32.11, -23.54) * mm});
            skArc(sketch, "E13.23.4", {"start": v(32.01, -24.35) * mm, "mid": v(32.17, -23.96) * mm, "end": v(32.11, -23.54) * mm});
            skLineSegment(sketch, "E13.23.5", {"start": v(32.01, -24.35) * mm, "end": v(31.9, -24.49) * mm});
            skLineSegment(sketch, "E13.23.6", {"start": v(31.8, -24.62) * mm, "end": v(31.9, -24.49) * mm});
            skArc(sketch, "E13.23.7", {"start": v(31.05, -24.93) * mm, "mid": v(31.47, -24.87) * mm, "end": v(31.8, -24.62) * mm});
            skArc(sketch, "E13.23.8", {"start": v(29.34, -24.54) * mm, "mid": v(30.19, -24.77) * mm, "end": v(31.05, -24.93) * mm});
            skArc(sketch, "E13.23.9", {"start": v(29.07, -24.39) * mm, "mid": v(29.2, -24.48) * mm, "end": v(29.34, -24.54) * mm});
            skArc(sketch, "E13.23.10", {"start": v(28.2, -23.65) * mm, "mid": v(27.6, -23.46) * mm, "end": v(27.04, -23.74) * mm});
            skLineSegment(sketch, "E13.23.11", {"start": v(29.07, -24.39) * mm, "end": v(28.2, -23.65) * mm});
            skArc(sketch, "E13.24.0", {"start": v(32.94, -14.47) * mm, "mid": v(32.93, -15.1) * mm, "end": v(33.35, -15.55) * mm});
            skLineSegment(sketch, "E13.24.1", {"start": v(34.39, -16.04) * mm, "end": v(33.35, -15.55) * mm});
            skArc(sketch, "E13.24.2", {"start": v(34.64, -16.22) * mm, "mid": v(34.52, -16.12) * mm, "end": v(34.39, -16.04) * mm});
            skArc(sketch, "E13.24.3", {"start": v(34.64, -16.22) * mm, "mid": v(35.21, -16.89) * mm, "end": v(35.71, -17.6) * mm});
            skArc(sketch, "E13.24.4", {"start": v(35.75, -18.42) * mm, "mid": v(35.84, -18) * mm, "end": v(35.71, -17.6) * mm});
            skLineSegment(sketch, "E13.24.5", {"start": v(35.75, -18.42) * mm, "end": v(35.68, -18.57) * mm});
            skLineSegment(sketch, "E13.24.6", {"start": v(35.6, -18.72) * mm, "end": v(35.68, -18.57) * mm});
            skArc(sketch, "E13.24.7", {"start": v(34.9, -19.16) * mm, "mid": v(35.3, -19.03) * mm, "end": v(35.6, -18.72) * mm});
            skArc(sketch, "E13.24.8", {"start": v(33.16, -19.07) * mm, "mid": v(34.03, -19.16) * mm, "end": v(34.9, -19.16) * mm});
            skArc(sketch, "E13.24.9", {"start": v(32.86, -18.97) * mm, "mid": v(33, -19.04) * mm, "end": v(33.16, -19.07) * mm});
            skArc(sketch, "E13.24.10", {"start": v(31.87, -18.4) * mm, "mid": v(31.25, -18.31) * mm, "end": v(30.75, -18.69) * mm});
            skLineSegment(sketch, "E13.24.11", {"start": v(32.86, -18.97) * mm, "end": v(31.87, -18.4) * mm});
            skArc(sketch, "E13.25.0", {"start": v(34.96, -8.53) * mm, "mid": v(35.05, -9.15) * mm, "end": v(35.55, -9.52) * mm});
            skLineSegment(sketch, "E13.25.1", {"start": v(36.65, -9.82) * mm, "end": v(35.55, -9.52) * mm});
            skArc(sketch, "E13.25.2", {"start": v(36.93, -9.96) * mm, "mid": v(36.8, -9.88) * mm, "end": v(36.65, -9.82) * mm});
            skArc(sketch, "E13.25.3", {"start": v(36.93, -9.96) * mm, "mid": v(37.6, -10.52) * mm, "end": v(38.23, -11.14) * mm});
            skArc(sketch, "E13.25.4", {"start": v(38.4, -11.93) * mm, "mid": v(38.42, -11.5) * mm, "end": v(38.23, -11.14) * mm});
            skLineSegment(sketch, "E13.25.5", {"start": v(38.4, -11.93) * mm, "end": v(38.36, -12.1) * mm});
            skLineSegment(sketch, "E13.25.6", {"start": v(38.3, -12.26) * mm, "end": v(38.36, -12.1) * mm});
            skArc(sketch, "E13.25.7", {"start": v(37.7, -12.8) * mm, "mid": v(38.08, -12.61) * mm, "end": v(38.3, -12.26) * mm});
            skArc(sketch, "E13.25.8", {"start": v(35.97, -13.03) * mm, "mid": v(36.84, -12.96) * mm, "end": v(37.7, -12.8) * mm});
            skArc(sketch, "E13.25.9", {"start": v(35.65, -12.98) * mm, "mid": v(35.8, -13.02) * mm, "end": v(35.97, -13.03) * mm});
            skArc(sketch, "E13.25.10", {"start": v(34.58, -12.59) * mm, "mid": v(33.96, -12.6) * mm, "end": v(33.53, -13.06) * mm});
            skLineSegment(sketch, "E13.25.11", {"start": v(35.65, -12.98) * mm, "end": v(34.58, -12.59) * mm});
            skArc(sketch, "E13.26.0", {"start": v(35.9, -2.33) * mm, "mid": v(36.1, -2.92) * mm, "end": v(36.66, -3.2) * mm});
            skLineSegment(sketch, "E13.26.1", {"start": v(37.8, -3.3) * mm, "end": v(36.66, -3.2) * mm});
            skArc(sketch, "E13.26.2", {"start": v(38.1, -3.4) * mm, "mid": v(37.95, -3.34) * mm, "end": v(37.8, -3.3) * mm});
            skArc(sketch, "E13.26.3", {"start": v(38.1, -3.4) * mm, "mid": v(38.86, -3.83) * mm, "end": v(39.58, -4.33) * mm});
            skArc(sketch, "E13.26.4", {"start": v(39.9, -5.08) * mm, "mid": v(39.84, -4.66) * mm, "end": v(39.58, -4.33) * mm});
            skLineSegment(sketch, "E13.26.5", {"start": v(39.9, -5.08) * mm, "end": v(39.88, -5.25) * mm});
            skLineSegment(sketch, "E13.26.6", {"start": v(39.85, -5.42) * mm, "end": v(39.88, -5.25) * mm});
            skArc(sketch, "E13.26.7", {"start": v(39.35, -6.06) * mm, "mid": v(39.69, -5.8) * mm, "end": v(39.85, -5.42) * mm});
            skArc(sketch, "E13.26.8", {"start": v(37.68, -6.58) * mm, "mid": v(38.53, -6.36) * mm, "end": v(39.35, -6.06) * mm});
            skArc(sketch, "E13.26.9", {"start": v(37.37, -6.59) * mm, "mid": v(37.52, -6.6) * mm, "end": v(37.68, -6.58) * mm});
            skArc(sketch, "E13.26.10", {"start": v(36.24, -6.4) * mm, "mid": v(35.63, -6.52) * mm, "end": v(35.29, -7.04) * mm});
            skLineSegment(sketch, "E13.26.11", {"start": v(37.37, -6.59) * mm, "end": v(36.24, -6.4) * mm});
            skArc(sketch, "E13.27.0", {"start": v(35.77, 3.94) * mm, "mid": v(36.06, 3.4) * mm, "end": v(36.66, 3.2) * mm});
            skLineSegment(sketch, "E13.27.1", {"start": v(37.8, 3.3) * mm, "end": v(36.66, 3.2) * mm});
            skArc(sketch, "E13.27.2", {"start": v(38.11, 3.27) * mm, "mid": v(37.96, 3.3) * mm, "end": v(37.8, 3.3) * mm});
            skArc(sketch, "E13.27.3", {"start": v(38.11, 3.27) * mm, "mid": v(38.94, 2.98) * mm, "end": v(39.73, 2.61) * mm});
            skArc(sketch, "E13.27.4", {"start": v(40.17, 1.93) * mm, "mid": v(40.04, 2.33) * mm, "end": v(39.73, 2.61) * mm});
            skLineSegment(sketch, "E13.27.5", {"start": v(40.17, 1.93) * mm, "end": v(40.18, 1.75) * mm});
            skLineSegment(sketch, "E13.27.6", {"start": v(40.19, 1.58) * mm, "end": v(40.18, 1.75) * mm});
            skArc(sketch, "E13.27.7", {"start": v(39.8, 0.86) * mm, "mid": v(40.1, 1.17) * mm, "end": v(40.19, 1.58) * mm});
            skArc(sketch, "E13.27.8", {"start": v(38.25, 0.06) * mm, "mid": v(39.05, 0.43) * mm, "end": v(39.8, 0.86) * mm});
            skArc(sketch, "E13.27.9", {"start": v(37.94, 0) * mm, "mid": v(38.1, 0.02) * mm, "end": v(38.25, 0.06) * mm});
            skArc(sketch, "E13.27.10", {"start": v(36.8, 0) * mm, "mid": v(36.22, -0.24) * mm, "end": v(35.97, -0.8) * mm});
            skLineSegment(sketch, "E13.27.11", {"start": v(37.94, 0) * mm, "end": v(36.8, 0) * mm});
            skArc(sketch, "E13.28.0", {"start": v(34.54, 10.1) * mm, "mid": v(34.93, 9.6) * mm, "end": v(35.55, 9.52) * mm});
            skLineSegment(sketch, "E13.28.1", {"start": v(36.65, 9.82) * mm, "end": v(35.55, 9.52) * mm});
            skArc(sketch, "E13.28.2", {"start": v(36.96, 9.84) * mm, "mid": v(36.8, 9.85) * mm, "end": v(36.65, 9.82) * mm});
            skArc(sketch, "E13.28.3", {"start": v(36.96, 9.84) * mm, "mid": v(37.83, 9.7) * mm, "end": v(38.67, 9.47) * mm});
            skArc(sketch, "E13.28.4", {"start": v(39.23, 8.87) * mm, "mid": v(39.03, 9.25) * mm, "end": v(38.67, 9.47) * mm});
            skLineSegment(sketch, "E13.28.5", {"start": v(39.23, 8.87) * mm, "end": v(39.27, 8.7) * mm});
            skLineSegment(sketch, "E13.28.6", {"start": v(39.3, 8.54) * mm, "end": v(39.27, 8.7) * mm});
            skArc(sketch, "E13.28.7", {"start": v(39.05, 7.76) * mm, "mid": v(39.28, 8.12) * mm, "end": v(39.3, 8.54) * mm});
            skArc(sketch, "E13.28.8", {"start": v(37.66, 6.7) * mm, "mid": v(38.38, 7.2) * mm, "end": v(39.05, 7.76) * mm});
            skArc(sketch, "E13.28.9", {"start": v(37.37, 6.59) * mm, "mid": v(37.52, 6.63) * mm, "end": v(37.66, 6.7) * mm});
            skArc(sketch, "E13.28.10", {"start": v(36.24, 6.4) * mm, "mid": v(35.71, 6.06) * mm, "end": v(35.57, 5.45) * mm});
            skLineSegment(sketch, "E13.28.11", {"start": v(37.37, 6.59) * mm, "end": v(36.24, 6.4) * mm});
            skArc(sketch, "E13.29.0", {"start": v(32.26, 15.93) * mm, "mid": v(32.73, 15.52) * mm, "end": v(33.35, 15.55) * mm});
            skLineSegment(sketch, "E13.29.1", {"start": v(34.39, 16.04) * mm, "end": v(33.35, 15.55) * mm});
            skArc(sketch, "E13.29.2", {"start": v(34.7, 16.11) * mm, "mid": v(34.54, 16.09) * mm, "end": v(34.39, 16.04) * mm});
            skArc(sketch, "E13.29.3", {"start": v(34.7, 16.11) * mm, "mid": v(35.57, 16.12) * mm, "end": v(36.44, 16.04) * mm});
            skArc(sketch, "E13.29.4", {"start": v(37.1, 15.55) * mm, "mid": v(36.83, 15.88) * mm, "end": v(36.44, 16.04) * mm});
            skLineSegment(sketch, "E13.29.5", {"start": v(37.1, 15.55) * mm, "end": v(37.16, 15.4) * mm});
            skLineSegment(sketch, "E13.29.6", {"start": v(37.22, 15.23) * mm, "end": v(37.16, 15.4) * mm});
            skArc(sketch, "E13.29.7", {"start": v(37.11, 14.43) * mm, "mid": v(37.27, 14.81) * mm, "end": v(37.22, 15.23) * mm});
            skArc(sketch, "E13.29.8", {"start": v(35.93, 13.14) * mm, "mid": v(36.55, 13.76) * mm, "end": v(37.11, 14.43) * mm});
            skArc(sketch, "E13.29.9", {"start": v(35.65, 12.98) * mm, "mid": v(35.8, 13.05) * mm, "end": v(35.93, 13.14) * mm});
            skArc(sketch, "E13.29.10", {"start": v(34.58, 12.59) * mm, "mid": v(34.12, 12.17) * mm, "end": v(34.08, 11.55) * mm});
            skLineSegment(sketch, "E13.29.11", {"start": v(35.65, 12.98) * mm, "end": v(34.58, 12.59) * mm});
            skArc(sketch, "E13.30.0", {"start": v(29, 21.3) * mm, "mid": v(29.54, 20.97) * mm, "end": v(30.14, 21.1) * mm});
            skLineSegment(sketch, "E13.30.1", {"start": v(31.08, 21.76) * mm, "end": v(30.14, 21.1) * mm});
            skArc(sketch, "E13.30.2", {"start": v(31.37, 21.9) * mm, "mid": v(31.22, 21.84) * mm, "end": v(31.08, 21.76) * mm});
            skArc(sketch, "E13.30.3", {"start": v(31.37, 21.9) * mm, "mid": v(32.23, 22.05) * mm, "end": v(33.1, 22.13) * mm});
            skArc(sketch, "E13.30.4", {"start": v(33.83, 21.76) * mm, "mid": v(33.51, 22.04) * mm, "end": v(33.1, 22.13) * mm});
            skLineSegment(sketch, "E13.30.5", {"start": v(33.83, 21.76) * mm, "end": v(33.92, 21.61) * mm});
            skLineSegment(sketch, "E13.30.6", {"start": v(34.01, 21.46) * mm, "end": v(33.92, 21.61) * mm});
            skArc(sketch, "E13.30.7", {"start": v(34.04, 20.65) * mm, "mid": v(34.14, 21.06) * mm, "end": v(34.01, 21.46) * mm});
            skArc(sketch, "E13.30.8", {"start": v(33.1, 19.18) * mm, "mid": v(33.6, 19.9) * mm, "end": v(34.04, 20.65) * mm});
            skArc(sketch, "E13.30.9", {"start": v(32.86, 18.97) * mm, "mid": v(32.99, 19.06) * mm, "end": v(33.1, 19.18) * mm});
            skArc(sketch, "E13.30.10", {"start": v(31.87, 18.4) * mm, "mid": v(31.49, 17.9) * mm, "end": v(31.56, 17.29) * mm});
            skLineSegment(sketch, "E13.30.11", {"start": v(32.86, 18.97) * mm, "end": v(31.87, 18.4) * mm});
            skArc(sketch, "E13.31.0", {"start": v(24.87, 26) * mm, "mid": v(25.45, 25.78) * mm, "end": v(26.02, 26.02) * mm});
            skLineSegment(sketch, "E13.31.1", {"start": v(26.83, 26.83) * mm, "end": v(26.02, 26.02) * mm});
            skArc(sketch, "E13.31.2", {"start": v(27.1, 27) * mm, "mid": v(26.95, 26.93) * mm, "end": v(26.83, 26.83) * mm});
            skArc(sketch, "E13.31.3", {"start": v(27.1, 27) * mm, "mid": v(27.91, 27.31) * mm, "end": v(28.76, 27.54) * mm});
            skArc(sketch, "E13.31.4", {"start": v(29.54, 27.3) * mm, "mid": v(29.18, 27.52) * mm, "end": v(28.76, 27.54) * mm});
            skLineSegment(sketch, "E13.31.5", {"start": v(29.54, 27.3) * mm, "end": v(29.65, 27.17) * mm});
            skLineSegment(sketch, "E13.31.6", {"start": v(29.77, 27.04) * mm, "end": v(29.65, 27.17) * mm});
            skArc(sketch, "E13.31.7", {"start": v(29.94, 26.25) * mm, "mid": v(29.96, 26.67) * mm, "end": v(29.77, 27.04) * mm});
            skArc(sketch, "E13.31.8", {"start": v(29.26, 24.63) * mm, "mid": v(29.64, 25.43) * mm, "end": v(29.94, 26.25) * mm});
            skArc(sketch, "E13.31.9", {"start": v(29.07, 24.39) * mm, "mid": v(29.18, 24.5) * mm, "end": v(29.26, 24.63) * mm});
            skArc(sketch, "E13.31.10", {"start": v(28.2, 23.65) * mm, "mid": v(27.9, 23.1) * mm, "end": v(28.08, 22.5) * mm});
            skLineSegment(sketch, "E13.31.11", {"start": v(29.07, 24.39) * mm, "end": v(28.2, 23.65) * mm});
            skArc(sketch, "E13.32.0", {"start": v(19.97, 29.93) * mm, "mid": v(20.58, 29.8) * mm, "end": v(21.1, 30.14) * mm});
            skLineSegment(sketch, "E13.32.1", {"start": v(21.76, 31.08) * mm, "end": v(21.1, 30.14) * mm});
            skArc(sketch, "E13.32.2", {"start": v(22, 31.3) * mm, "mid": v(21.87, 31.2) * mm, "end": v(21.76, 31.08) * mm});
            skArc(sketch, "E13.32.3", {"start": v(22, 31.3) * mm, "mid": v(22.75, 31.74) * mm, "end": v(23.54, 32.11) * mm});
            skArc(sketch, "E13.32.4", {"start": v(24.35, 32.01) * mm, "mid": v(23.96, 32.17) * mm, "end": v(23.54, 32.11) * mm});
            skLineSegment(sketch, "E13.32.5", {"start": v(24.35, 32.01) * mm, "end": v(24.49, 31.9) * mm});
            skLineSegment(sketch, "E13.32.6", {"start": v(24.62, 31.8) * mm, "end": v(24.49, 31.9) * mm});
            skArc(sketch, "E13.32.7", {"start": v(24.93, 31.05) * mm, "mid": v(24.87, 31.47) * mm, "end": v(24.62, 31.8) * mm});
            skArc(sketch, "E13.32.8", {"start": v(24.54, 29.34) * mm, "mid": v(24.77, 30.19) * mm, "end": v(24.93, 31.05) * mm});
            skArc(sketch, "E13.32.9", {"start": v(24.39, 29.07) * mm, "mid": v(24.48, 29.2) * mm, "end": v(24.54, 29.34) * mm});
            skArc(sketch, "E13.32.10", {"start": v(23.65, 28.2) * mm, "mid": v(23.46, 27.6) * mm, "end": v(23.74, 27.04) * mm});
            skLineSegment(sketch, "E13.32.11", {"start": v(24.39, 29.07) * mm, "end": v(23.65, 28.2) * mm});
            skArc(sketch, "E13.33.0", {"start": v(14.47, 32.94) * mm, "mid": v(15.1, 32.93) * mm, "end": v(15.55, 33.35) * mm});
            skLineSegment(sketch, "E13.33.1", {"start": v(16.04, 34.39) * mm, "end": v(15.55, 33.35) * mm});
            skArc(sketch, "E13.33.2", {"start": v(16.22, 34.64) * mm, "mid": v(16.12, 34.52) * mm, "end": v(16.04, 34.39) * mm});
            skArc(sketch, "E13.33.3", {"start": v(16.22, 34.64) * mm, "mid": v(16.89, 35.21) * mm, "end": v(17.6, 35.71) * mm});
            skArc(sketch, "E13.33.4", {"start": v(18.42, 35.75) * mm, "mid": v(18, 35.84) * mm, "end": v(17.6, 35.71) * mm});
            skLineSegment(sketch, "E13.33.5", {"start": v(18.42, 35.75) * mm, "end": v(18.57, 35.68) * mm});
            skLineSegment(sketch, "E13.33.6", {"start": v(18.72, 35.6) * mm, "end": v(18.57, 35.68) * mm});
            skArc(sketch, "E13.33.7", {"start": v(19.16, 34.9) * mm, "mid": v(19.03, 35.3) * mm, "end": v(18.72, 35.6) * mm});
            skArc(sketch, "E13.33.8", {"start": v(19.07, 33.16) * mm, "mid": v(19.16, 34.03) * mm, "end": v(19.16, 34.9) * mm});
            skArc(sketch, "E13.33.9", {"start": v(18.97, 32.86) * mm, "mid": v(19.04, 33) * mm, "end": v(19.07, 33.16) * mm});
            skArc(sketch, "E13.33.10", {"start": v(18.4, 31.87) * mm, "mid": v(18.31, 31.25) * mm, "end": v(18.69, 30.75) * mm});
            skLineSegment(sketch, "E13.33.11", {"start": v(18.97, 32.86) * mm, "end": v(18.4, 31.87) * mm});
            skArc(sketch, "E13.34.0", {"start": v(8.53, 34.96) * mm, "mid": v(9.15, 35.05) * mm, "end": v(9.52, 35.55) * mm});
            skLineSegment(sketch, "E13.34.1", {"start": v(9.82, 36.65) * mm, "end": v(9.52, 35.55) * mm});
            skArc(sketch, "E13.34.2", {"start": v(9.96, 36.93) * mm, "mid": v(9.88, 36.8) * mm, "end": v(9.82, 36.65) * mm});
            skArc(sketch, "E13.34.3", {"start": v(9.96, 36.93) * mm, "mid": v(10.52, 37.6) * mm, "end": v(11.14, 38.23) * mm});
            skArc(sketch, "E13.34.4", {"start": v(11.93, 38.4) * mm, "mid": v(11.5, 38.42) * mm, "end": v(11.14, 38.23) * mm});
            skLineSegment(sketch, "E13.34.5", {"start": v(11.93, 38.4) * mm, "end": v(12.1, 38.36) * mm});
            skLineSegment(sketch, "E13.34.6", {"start": v(12.26, 38.3) * mm, "end": v(12.1, 38.36) * mm});
            skArc(sketch, "E13.34.7", {"start": v(12.8, 37.7) * mm, "mid": v(12.61, 38.08) * mm, "end": v(12.26, 38.3) * mm});
            skArc(sketch, "E13.34.8", {"start": v(13.03, 35.97) * mm, "mid": v(12.96, 36.84) * mm, "end": v(12.8, 37.7) * mm});
            skArc(sketch, "E13.34.9", {"start": v(12.98, 35.65) * mm, "mid": v(13.02, 35.8) * mm, "end": v(13.03, 35.97) * mm});
            skArc(sketch, "E13.34.10", {"start": v(12.59, 34.58) * mm, "mid": v(12.6, 33.96) * mm, "end": v(13.06, 33.53) * mm});
            skLineSegment(sketch, "E13.34.11", {"start": v(12.98, 35.65) * mm, "end": v(12.59, 34.58) * mm});
            skArc(sketch, "E13.35.0", {"start": v(2.33, 35.9) * mm, "mid": v(2.92, 36.1) * mm, "end": v(3.2, 36.66) * mm});
            skLineSegment(sketch, "E13.35.1", {"start": v(3.3, 37.8) * mm, "end": v(3.2, 36.66) * mm});
            skArc(sketch, "E13.35.2", {"start": v(3.4, 38.1) * mm, "mid": v(3.34, 37.95) * mm, "end": v(3.3, 37.8) * mm});
            skArc(sketch, "E13.35.3", {"start": v(3.4, 38.1) * mm, "mid": v(3.83, 38.86) * mm, "end": v(4.33, 39.58) * mm});
            skArc(sketch, "E13.35.4", {"start": v(5.08, 39.9) * mm, "mid": v(4.66, 39.84) * mm, "end": v(4.33, 39.58) * mm});
            skLineSegment(sketch, "E13.35.5", {"start": v(5.08, 39.9) * mm, "end": v(5.25, 39.88) * mm});
            skLineSegment(sketch, "E13.35.6", {"start": v(5.42, 39.85) * mm, "end": v(5.25, 39.88) * mm});
            skArc(sketch, "E13.35.7", {"start": v(6.06, 39.35) * mm, "mid": v(5.8, 39.69) * mm, "end": v(5.42, 39.85) * mm});
            skArc(sketch, "E13.35.8", {"start": v(6.58, 37.68) * mm, "mid": v(6.36, 38.53) * mm, "end": v(6.06, 39.35) * mm});
            skArc(sketch, "E13.35.9", {"start": v(6.59, 37.37) * mm, "mid": v(6.6, 37.52) * mm, "end": v(6.58, 37.68) * mm});
            skArc(sketch, "E13.35.10", {"start": v(6.4, 36.24) * mm, "mid": v(6.52, 35.63) * mm, "end": v(7.04, 35.29) * mm});
            skLineSegment(sketch, "E13.35.11", {"start": v(6.59, 37.37) * mm, "end": v(6.4, 36.24) * mm});
            skArc(sketch, "E14.trimOffspring", {"start": v(2.33, 35.9) * mm, "mid": v(1.57, 35.95) * mm, "end": v(0.8, 35.97) * mm});
            skArc(sketch, "E15.trimOffspring", {"start": v(8.53, 34.96) * mm, "mid": v(7.79, 35.13) * mm, "end": v(7.04, 35.29) * mm});
            skArc(sketch, "E16.trimOffspring", {"start": v(14.47, 32.94) * mm, "mid": v(13.77, 33.24) * mm, "end": v(13.06, 33.53) * mm});
            skArc(sketch, "E17.trimOffspring", {"start": v(19.97, 29.93) * mm, "mid": v(19.33, 30.35) * mm, "end": v(18.69, 30.75) * mm});
            skArc(sketch, "E18.trimOffspring", {"start": v(-10.1, 34.54) * mm, "mid": v(-10.82, 34.32) * mm, "end": v(-11.55, 34.08) * mm});
            skArc(sketch, "E19.trimOffspring", {"start": v(-15.93, 32.26) * mm, "mid": v(-16.62, 31.92) * mm, "end": v(-17.29, 31.56) * mm});
            skArc(sketch, "E20.trimOffspring", {"start": v(-21.3, 29) * mm, "mid": v(-21.9, 28.55) * mm, "end": v(-22.5, 28.08) * mm});
            skArc(sketch, "E21.trimOffspring", {"start": v(-26, 24.87) * mm, "mid": v(-26.53, 24.3) * mm, "end": v(-27.04, 23.74) * mm});
            skArc(sketch, "E22.trimOffspring", {"start": v(24.87, 26) * mm, "mid": v(24.3, 26.53) * mm, "end": v(23.74, 27.04) * mm});
            skArc(sketch, "E23.trimOffspring", {"start": v(29, 21.3) * mm, "mid": v(28.55, 21.9) * mm, "end": v(28.08, 22.5) * mm});
            skArc(sketch, "E24.trimOffspring", {"start": v(32.26, 15.93) * mm, "mid": v(31.92, 16.62) * mm, "end": v(31.56, 17.29) * mm});
            skArc(sketch, "E25.trimOffspring", {"start": v(34.54, 10.1) * mm, "mid": v(34.32, 10.82) * mm, "end": v(34.08, 11.55) * mm});
            skArc(sketch, "E26.trimOffspring", {"start": v(35.77, 3.94) * mm, "mid": v(35.68, 4.7) * mm, "end": v(35.57, 5.45) * mm});
            skArc(sketch, "E27.trimOffspring", {"start": v(35.9, -2.33) * mm, "mid": v(35.95, -1.57) * mm, "end": v(35.97, -0.8) * mm});
            skArc(sketch, "E28.trimOffspring", {"start": v(34.96, -8.53) * mm, "mid": v(35.13, -7.79) * mm, "end": v(35.29, -7.04) * mm});
            skArc(sketch, "E29.trimOffspring", {"start": v(-29.93, 19.97) * mm, "mid": v(-30.35, 19.33) * mm, "end": v(-30.75, 18.69) * mm});
            skArc(sketch, "E30.trimOffspring", {"start": v(-32.94, 14.47) * mm, "mid": v(-33.24, 13.77) * mm, "end": v(-33.53, 13.06) * mm});
            skArc(sketch, "E31.trimOffspring", {"start": v(-34.96, 8.53) * mm, "mid": v(-35.13, 7.79) * mm, "end": v(-35.29, 7.04) * mm});
            skArc(sketch, "E32.trimOffspring", {"start": v(-35.9, 2.33) * mm, "mid": v(-35.95, 1.57) * mm, "end": v(-35.97, 0.8) * mm});
            skArc(sketch, "E33.trimOffspring", {"start": v(-35.77, -3.94) * mm, "mid": v(-35.68, -4.7) * mm, "end": v(-35.57, -5.45) * mm});
            skArc(sketch, "E34.trimOffspring", {"start": v(-34.54, -10.1) * mm, "mid": v(-34.32, -10.82) * mm, "end": v(-34.08, -11.55) * mm});
            skArc(sketch, "E35.trimOffspring", {"start": v(-32.26, -15.93) * mm, "mid": v(-31.92, -16.62) * mm, "end": v(-31.56, -17.29) * mm});
            skArc(sketch, "E36.trimOffspring", {"start": v(-29, -21.3) * mm, "mid": v(-28.55, -21.9) * mm, "end": v(-28.08, -22.5) * mm});
            skArc(sketch, "E37.trimOffspring", {"start": v(-24.87, -26) * mm, "mid": v(-24.3, -26.53) * mm, "end": v(-23.74, -27.04) * mm});
            skArc(sketch, "E38.trimOffspring", {"start": v(-19.97, -29.93) * mm, "mid": v(-19.33, -30.35) * mm, "end": v(-18.69, -30.75) * mm});
            skArc(sketch, "E39.trimOffspring", {"start": v(-14.47, -32.94) * mm, "mid": v(-13.77, -33.24) * mm, "end": v(-13.06, -33.53) * mm});
            skArc(sketch, "E40.trimOffspring", {"start": v(-8.53, -34.96) * mm, "mid": v(-7.79, -35.13) * mm, "end": v(-7.04, -35.29) * mm});
            skArc(sketch, "E41.trimOffspring", {"start": v(-2.33, -35.9) * mm, "mid": v(-1.57, -35.95) * mm, "end": v(-0.8, -35.97) * mm});
            skArc(sketch, "E42.trimOffspring", {"start": v(3.94, -35.77) * mm, "mid": v(4.7, -35.68) * mm, "end": v(5.45, -35.57) * mm});
            skArc(sketch, "E43.trimOffspring", {"start": v(10.1, -34.54) * mm, "mid": v(10.82, -34.32) * mm, "end": v(11.55, -34.08) * mm});
            skArc(sketch, "E44.trimOffspring", {"start": v(15.93, -32.26) * mm, "mid": v(16.62, -31.92) * mm, "end": v(17.29, -31.56) * mm});
            skArc(sketch, "E45.trimOffspring", {"start": v(21.3, -29) * mm, "mid": v(21.9, -28.55) * mm, "end": v(22.5, -28.08) * mm});
            skArc(sketch, "E46.trimOffspring", {"start": v(26, -24.87) * mm, "mid": v(26.53, -24.3) * mm, "end": v(27.04, -23.74) * mm});
            skArc(sketch, "E47.trimOffspring", {"start": v(29.93, -19.97) * mm, "mid": v(30.35, -19.33) * mm, "end": v(30.75, -18.69) * mm});
            skArc(sketch, "E48.trimOffspring", {"start": v(32.94, -14.47) * mm, "mid": v(33.24, -13.77) * mm, "end": v(33.53, -13.06) * mm});
            skSolve(sketch);
        }
        {
            var Q0;
            Q0 = qSketchRegion(id + "F0", true);
            extrude(context, id + "F1", {"entities" : qUnion([Q0]), "depth" : 12.7 * mm});
        }
        {
            var Q0;
            Q0=makeQuery(id+"F1.opExtrude","CAP_FACE",FACE,{"disambiguationData":[OSD([sQuery(id+"F0.wireOp",EDGE,"E0"),sQuery(id+"F0.wireOp",EDGE,"E1"),sQuery(id+"F0.wireOp",EDGE,"E2"),sQuery(id+"F0.wireOp",EDGE,"E3"),sQuery(id+"F0.wireOp",EDGE,"E4.MirrorCS"),sQuery(id+"F0.wireOp",EDGE,"E5.MirrorCS"),sQuery(id+"F0.wireOp",EDGE,"E6.MirrorCS"),sQuery(id+"F0.wireOp",EDGE,"E7.filletArc"),sQuery(id+"F0.wireOp",EDGE,"E8.filletArc"),sQuery(id+"F0.wireOp",EDGE,"E9.filletArc"),sQuery(id+"F0.wireOp",EDGE,"E10.filletArc"),sQuery(id+"F0.wireOp",EDGE,"E11.filletArc"),sQuery(id+"F0.wireOp",EDGE,"E12.filletArc"),sQuery(id+"F0.wireOp",EDGE,"E13.1.0"),sQuery(id+"F0.wireOp",EDGE,"E13.1.1"),sQuery(id+"F0.wireOp",EDGE,"E13.1.2"),sQuery(id+"F0.wireOp",EDGE,"E13.1.3"),sQuery(id+"F0.wireOp",EDGE,"E13.1.4"),sQuery(id+"F0.wireOp",EDGE,"E13.1.5"),sQuery(id+"F0.wireOp",EDGE,"E13.1.6"),sQuery(id+"F0.wireOp",EDGE,"E13.1.7"),sQuery(id+"F0.wireOp",EDGE,"E13.1.8"),sQuery(id+"F0.wireOp",EDGE,"E13.1.9"),sQuery(id+"F0.wireOp",EDGE,"E13.1.10"),sQuery(id+"F0.wireOp",EDGE,"E13.1.11"),sQuery(id+"F0.wireOp",EDGE,"E13.2.0"),sQuery(id+"F0.wireOp",EDGE,"E13.2.1"),sQuery(id+"F0.wireOp",EDGE,"E13.2.2"),sQuery(id+"F0.wireOp",EDGE,"E13.2.3"),sQuery(id+"F0.wireOp",EDGE,"E13.2.4"),sQuery(id+"F0.wireOp",EDGE,"E13.2.5"),sQuery(id+"F0.wireOp",EDGE,"E13.2.6"),sQuery(id+"F0.wireOp",EDGE,"E13.2.7"),sQuery(id+"F0.wireOp",EDGE,"E13.2.8"),sQuery(id+"F0.wireOp",EDGE,"E13.2.9"),sQuery(id+"F0.wireOp",EDGE,"E13.2.10"),sQuery(id+"F0.wireOp",EDGE,"E13.2.11"),sQuery(id+"F0.wireOp",EDGE,"E13.3.0"),sQuery(id+"F0.wireOp",EDGE,"E13.3.1"),sQuery(id+"F0.wireOp",EDGE,"E13.3.2"),sQuery(id+"F0.wireOp",EDGE,"E13.3.3"),sQuery(id+"F0.wireOp",EDGE,"E13.3.4"),sQuery(id+"F0.wireOp",EDGE,"E13.3.5"),sQuery(id+"F0.wireOp",EDGE,"E13.3.6"),sQuery(id+"F0.wireOp",EDGE,"E13.3.7"),sQuery(id+"F0.wireOp",EDGE,"E13.3.8"),sQuery(id+"F0.wireOp",EDGE,"E13.3.9"),sQuery(id+"F0.wireOp",EDGE,"E13.3.10"),sQuery(id+"F0.wireOp",EDGE,"E13.3.11"),sQuery(id+"F0.wireOp",EDGE,"E13.4.0"),sQuery(id+"F0.wireOp",EDGE,"E13.4.1"),sQuery(id+"F0.wireOp",EDGE,"E13.4.2"),sQuery(id+"F0.wireOp",EDGE,"E13.4.3"),sQuery(id+"F0.wireOp",EDGE,"E13.4.4"),sQuery(id+"F0.wireOp",EDGE,"E13.4.5"),sQuery(id+"F0.wireOp",EDGE,"E13.4.6"),sQuery(id+"F0.wireOp",EDGE,"E13.4.7"),sQuery(id+"F0.wireOp",EDGE,"E13.4.8"),sQuery(id+"F0.wireOp",EDGE,"E13.4.9"),sQuery(id+"F0.wireOp",EDGE,"E13.4.10"),sQuery(id+"F0.wireOp",EDGE,"E13.4.11"),sQuery(id+"F0.wireOp",EDGE,"E13.5.0"),sQuery(id+"F0.wireOp",EDGE,"E13.5.1"),sQuery(id+"F0.wireOp",EDGE,"E13.5.2"),sQuery(id+"F0.wireOp",EDGE,"E13.5.3"),sQuery(id+"F0.wireOp",EDGE,"E13.5.4"),sQuery(id+"F0.wireOp",EDGE,"E13.5.5"),sQuery(id+"F0.wireOp",EDGE,"E13.5.6"),sQuery(id+"F0.wireOp",EDGE,"E13.5.7"),sQuery(id+"F0.wireOp",EDGE,"E13.5.8"),sQuery(id+"F0.wireOp",EDGE,"E13.5.9"),sQuery(id+"F0.wireOp",EDGE,"E13.5.10"),sQuery(id+"F0.wireOp",EDGE,"E13.5.11"),sQuery(id+"F0.wireOp",EDGE,"E13.6.0"),sQuery(id+"F0.wireOp",EDGE,"E13.6.1"),sQuery(id+"F0.wireOp",EDGE,"E13.6.2"),sQuery(id+"F0.wireOp",EDGE,"E13.6.3"),sQuery(id+"F0.wireOp",EDGE,"E13.6.4"),sQuery(id+"F0.wireOp",EDGE,"E13.6.5"),sQuery(id+"F0.wireOp",EDGE,"E13.6.6"),sQuery(id+"F0.wireOp",EDGE,"E13.6.7"),sQuery(id+"F0.wireOp",EDGE,"E13.6.8"),sQuery(id+"F0.wireOp",EDGE,"E13.6.9"),sQuery(id+"F0.wireOp",EDGE,"E13.6.10"),sQuery(id+"F0.wireOp",EDGE,"E13.6.11"),sQuery(id+"F0.wireOp",EDGE,"E13.7.0"),sQuery(id+"F0.wireOp",EDGE,"E13.7.1"),sQuery(id+"F0.wireOp",EDGE,"E13.7.2"),sQuery(id+"F0.wireOp",EDGE,"E13.7.3"),sQuery(id+"F0.wireOp",EDGE,"E13.7.4"),sQuery(id+"F0.wireOp",EDGE,"E13.7.5"),sQuery(id+"F0.wireOp",EDGE,"E13.7.6"),sQuery(id+"F0.wireOp",EDGE,"E13.7.7"),sQuery(id+"F0.wireOp",EDGE,"E13.7.8"),sQuery(id+"F0.wireOp",EDGE,"E13.7.9"),sQuery(id+"F0.wireOp",EDGE,"E13.7.10"),sQuery(id+"F0.wireOp",EDGE,"E13.7.11"),sQuery(id+"F0.wireOp",EDGE,"E13.8.0"),sQuery(id+"F0.wireOp",EDGE,"E13.8.1"),sQuery(id+"F0.wireOp",EDGE,"E13.8.2"),sQuery(id+"F0.wireOp",EDGE,"E13.8.3"),sQuery(id+"F0.wireOp",EDGE,"E13.8.4"),sQuery(id+"F0.wireOp",EDGE,"E13.8.5"),sQuery(id+"F0.wireOp",EDGE,"E13.8.6"),sQuery(id+"F0.wireOp",EDGE,"E13.8.7"),sQuery(id+"F0.wireOp",EDGE,"E13.8.8"),sQuery(id+"F0.wireOp",EDGE,"E13.8.9"),sQuery(id+"F0.wireOp",EDGE,"E13.8.10"),sQuery(id+"F0.wireOp",EDGE,"E13.8.11"),sQuery(id+"F0.wireOp",EDGE,"E13.9.0"),sQuery(id+"F0.wireOp",EDGE,"E13.9.1"),sQuery(id+"F0.wireOp",EDGE,"E13.9.2"),sQuery(id+"F0.wireOp",EDGE,"E13.9.3"),sQuery(id+"F0.wireOp",EDGE,"E13.9.4"),sQuery(id+"F0.wireOp",EDGE,"E13.9.5"),sQuery(id+"F0.wireOp",EDGE,"E13.9.6"),sQuery(id+"F0.wireOp",EDGE,"E13.9.7"),sQuery(id+"F0.wireOp",EDGE,"E13.9.8"),sQuery(id+"F0.wireOp",EDGE,"E13.9.9"),sQuery(id+"F0.wireOp",EDGE,"E13.9.10"),sQuery(id+"F0.wireOp",EDGE,"E13.9.11"),sQuery(id+"F0.wireOp",EDGE,"E13.10.0"),sQuery(id+"F0.wireOp",EDGE,"E13.10.1"),sQuery(id+"F0.wireOp",EDGE,"E13.10.2"),sQuery(id+"F0.wireOp",EDGE,"E13.10.3"),sQuery(id+"F0.wireOp",EDGE,"E13.10.4"),sQuery(id+"F0.wireOp",EDGE,"E13.10.5"),sQuery(id+"F0.wireOp",EDGE,"E13.10.6"),sQuery(id+"F0.wireOp",EDGE,"E13.10.7"),sQuery(id+"F0.wireOp",EDGE,"E13.10.8"),sQuery(id+"F0.wireOp",EDGE,"E13.10.9"),sQuery(id+"F0.wireOp",EDGE,"E13.10.10"),sQuery(id+"F0.wireOp",EDGE,"E13.10.11"),sQuery(id+"F0.wireOp",EDGE,"E13.11.0"),sQuery(id+"F0.wireOp",EDGE,"E13.11.1"),sQuery(id+"F0.wireOp",EDGE,"E13.11.2"),sQuery(id+"F0.wireOp",EDGE,"E13.11.3"),sQuery(id+"F0.wireOp",EDGE,"E13.11.4"),sQuery(id+"F0.wireOp",EDGE,"E13.11.5"),sQuery(id+"F0.wireOp",EDGE,"E13.11.6"),sQuery(id+"F0.wireOp",EDGE,"E13.11.7"),sQuery(id+"F0.wireOp",EDGE,"E13.11.8"),sQuery(id+"F0.wireOp",EDGE,"E13.11.9"),sQuery(id+"F0.wireOp",EDGE,"E13.11.10"),sQuery(id+"F0.wireOp",EDGE,"E13.11.11"),sQuery(id+"F0.wireOp",EDGE,"E13.12.0"),sQuery(id+"F0.wireOp",EDGE,"E13.12.1"),sQuery(id+"F0.wireOp",EDGE,"E13.12.2"),sQuery(id+"F0.wireOp",EDGE,"E13.12.3"),sQuery(id+"F0.wireOp",EDGE,"E13.12.4"),sQuery(id+"F0.wireOp",EDGE,"E13.12.5"),sQuery(id+"F0.wireOp",EDGE,"E13.12.6"),sQuery(id+"F0.wireOp",EDGE,"E13.12.7"),sQuery(id+"F0.wireOp",EDGE,"E13.12.8"),sQuery(id+"F0.wireOp",EDGE,"E13.12.9"),sQuery(id+"F0.wireOp",EDGE,"E13.12.10"),sQuery(id+"F0.wireOp",EDGE,"E13.12.11"),sQuery(id+"F0.wireOp",EDGE,"E13.13.0"),sQuery(id+"F0.wireOp",EDGE,"E13.13.1"),sQuery(id+"F0.wireOp",EDGE,"E13.13.2"),sQuery(id+"F0.wireOp",EDGE,"E13.13.3"),sQuery(id+"F0.wireOp",EDGE,"E13.13.4"),sQuery(id+"F0.wireOp",EDGE,"E13.13.5"),sQuery(id+"F0.wireOp",EDGE,"E13.13.6"),sQuery(id+"F0.wireOp",EDGE,"E13.13.7"),sQuery(id+"F0.wireOp",EDGE,"E13.13.8"),sQuery(id+"F0.wireOp",EDGE,"E13.13.9"),sQuery(id+"F0.wireOp",EDGE,"E13.13.10"),sQuery(id+"F0.wireOp",EDGE,"E13.13.11"),sQuery(id+"F0.wireOp",EDGE,"E13.14.0"),sQuery(id+"F0.wireOp",EDGE,"E13.14.1"),sQuery(id+"F0.wireOp",EDGE,"E13.14.2"),sQuery(id+"F0.wireOp",EDGE,"E13.14.3"),sQuery(id+"F0.wireOp",EDGE,"E13.14.4"),sQuery(id+"F0.wireOp",EDGE,"E13.14.5"),sQuery(id+"F0.wireOp",EDGE,"E13.14.6"),sQuery(id+"F0.wireOp",EDGE,"E13.14.7"),sQuery(id+"F0.wireOp",EDGE,"E13.14.8"),sQuery(id+"F0.wireOp",EDGE,"E13.14.9"),sQuery(id+"F0.wireOp",EDGE,"E13.14.10"),sQuery(id+"F0.wireOp",EDGE,"E13.14.11"),sQuery(id+"F0.wireOp",EDGE,"E13.15.0"),sQuery(id+"F0.wireOp",EDGE,"E13.15.1"),sQuery(id+"F0.wireOp",EDGE,"E13.15.2"),sQuery(id+"F0.wireOp",EDGE,"E13.15.3"),sQuery(id+"F0.wireOp",EDGE,"E13.15.4"),sQuery(id+"F0.wireOp",EDGE,"E13.15.5"),sQuery(id+"F0.wireOp",EDGE,"E13.15.6"),sQuery(id+"F0.wireOp",EDGE,"E13.15.7"),sQuery(id+"F0.wireOp",EDGE,"E13.15.8"),sQuery(id+"F0.wireOp",EDGE,"E13.15.9"),sQuery(id+"F0.wireOp",EDGE,"E13.15.10"),sQuery(id+"F0.wireOp",EDGE,"E13.15.11"),sQuery(id+"F0.wireOp",EDGE,"E13.16.0"),sQuery(id+"F0.wireOp",EDGE,"E13.16.1"),sQuery(id+"F0.wireOp",EDGE,"E13.16.2"),sQuery(id+"F0.wireOp",EDGE,"E13.16.3"),sQuery(id+"F0.wireOp",EDGE,"E13.16.4"),sQuery(id+"F0.wireOp",EDGE,"E13.16.5"),sQuery(id+"F0.wireOp",EDGE,"E13.16.6"),sQuery(id+"F0.wireOp",EDGE,"E13.16.7"),sQuery(id+"F0.wireOp",EDGE,"E13.16.8"),sQuery(id+"F0.wireOp",EDGE,"E13.16.9"),sQuery(id+"F0.wireOp",EDGE,"E13.16.10"),sQuery(id+"F0.wireOp",EDGE,"E13.16.11"),sQuery(id+"F0.wireOp",EDGE,"E13.17.0"),sQuery(id+"F0.wireOp",EDGE,"E13.17.1"),sQuery(id+"F0.wireOp",EDGE,"E13.17.2"),sQuery(id+"F0.wireOp",EDGE,"E13.17.3"),sQuery(id+"F0.wireOp",EDGE,"E13.17.4"),sQuery(id+"F0.wireOp",EDGE,"E13.17.5"),sQuery(id+"F0.wireOp",EDGE,"E13.17.6"),sQuery(id+"F0.wireOp",EDGE,"E13.17.7"),sQuery(id+"F0.wireOp",EDGE,"E13.17.8"),sQuery(id+"F0.wireOp",EDGE,"E13.17.9"),sQuery(id+"F0.wireOp",EDGE,"E13.17.10"),sQuery(id+"F0.wireOp",EDGE,"E13.17.11"),sQuery(id+"F0.wireOp",EDGE,"E13.18.0"),sQuery(id+"F0.wireOp",EDGE,"E13.18.1"),sQuery(id+"F0.wireOp",EDGE,"E13.18.2"),sQuery(id+"F0.wireOp",EDGE,"E13.18.3"),sQuery(id+"F0.wireOp",EDGE,"E13.18.4"),sQuery(id+"F0.wireOp",EDGE,"E13.18.5"),sQuery(id+"F0.wireOp",EDGE,"E13.18.6"),sQuery(id+"F0.wireOp",EDGE,"E13.18.7"),sQuery(id+"F0.wireOp",EDGE,"E13.18.8"),sQuery(id+"F0.wireOp",EDGE,"E13.18.9"),sQuery(id+"F0.wireOp",EDGE,"E13.18.10"),sQuery(id+"F0.wireOp",EDGE,"E13.18.11"),sQuery(id+"F0.wireOp",EDGE,"E13.19.0"),sQuery(id+"F0.wireOp",EDGE,"E13.19.1"),sQuery(id+"F0.wireOp",EDGE,"E13.19.2"),sQuery(id+"F0.wireOp",EDGE,"E13.19.3"),sQuery(id+"F0.wireOp",EDGE,"E13.19.4"),sQuery(id+"F0.wireOp",EDGE,"E13.19.5"),sQuery(id+"F0.wireOp",EDGE,"E13.19.6"),sQuery(id+"F0.wireOp",EDGE,"E13.19.7"),sQuery(id+"F0.wireOp",EDGE,"E13.19.8"),sQuery(id+"F0.wireOp",EDGE,"E13.19.9"),sQuery(id+"F0.wireOp",EDGE,"E13.19.10"),sQuery(id+"F0.wireOp",EDGE,"E13.19.11"),sQuery(id+"F0.wireOp",EDGE,"E13.20.0"),sQuery(id+"F0.wireOp",EDGE,"E13.20.1"),sQuery(id+"F0.wireOp",EDGE,"E13.20.2"),sQuery(id+"F0.wireOp",EDGE,"E13.20.3"),sQuery(id+"F0.wireOp",EDGE,"E13.20.4"),sQuery(id+"F0.wireOp",EDGE,"E13.20.5"),sQuery(id+"F0.wireOp",EDGE,"E13.20.6"),sQuery(id+"F0.wireOp",EDGE,"E13.20.7"),sQuery(id+"F0.wireOp",EDGE,"E13.20.8"),sQuery(id+"F0.wireOp",EDGE,"E13.20.9"),sQuery(id+"F0.wireOp",EDGE,"E13.20.10"),sQuery(id+"F0.wireOp",EDGE,"E13.20.11"),sQuery(id+"F0.wireOp",EDGE,"E13.21.0"),sQuery(id+"F0.wireOp",EDGE,"E13.21.1"),sQuery(id+"F0.wireOp",EDGE,"E13.21.2"),sQuery(id+"F0.wireOp",EDGE,"E13.21.3"),sQuery(id+"F0.wireOp",EDGE,"E13.21.4"),sQuery(id+"F0.wireOp",EDGE,"E13.21.5"),sQuery(id+"F0.wireOp",EDGE,"E13.21.6"),sQuery(id+"F0.wireOp",EDGE,"E13.21.7"),sQuery(id+"F0.wireOp",EDGE,"E13.21.8"),sQuery(id+"F0.wireOp",EDGE,"E13.21.9"),sQuery(id+"F0.wireOp",EDGE,"E13.21.10"),sQuery(id+"F0.wireOp",EDGE,"E13.21.11"),sQuery(id+"F0.wireOp",EDGE,"E13.22.0"),sQuery(id+"F0.wireOp",EDGE,"E13.22.1"),sQuery(id+"F0.wireOp",EDGE,"E13.22.2"),sQuery(id+"F0.wireOp",EDGE,"E13.22.3"),sQuery(id+"F0.wireOp",EDGE,"E13.22.4"),sQuery(id+"F0.wireOp",EDGE,"E13.22.5"),sQuery(id+"F0.wireOp",EDGE,"E13.22.6"),sQuery(id+"F0.wireOp",EDGE,"E13.22.7"),sQuery(id+"F0.wireOp",EDGE,"E13.22.8"),sQuery(id+"F0.wireOp",EDGE,"E13.22.9"),sQuery(id+"F0.wireOp",EDGE,"E13.22.10"),sQuery(id+"F0.wireOp",EDGE,"E13.22.11"),sQuery(id+"F0.wireOp",EDGE,"E13.23.0"),sQuery(id+"F0.wireOp",EDGE,"E13.23.1"),sQuery(id+"F0.wireOp",EDGE,"E13.23.2"),sQuery(id+"F0.wireOp",EDGE,"E13.23.3"),sQuery(id+"F0.wireOp",EDGE,"E13.23.4"),sQuery(id+"F0.wireOp",EDGE,"E13.23.5"),sQuery(id+"F0.wireOp",EDGE,"E13.23.6"),sQuery(id+"F0.wireOp",EDGE,"E13.23.7"),sQuery(id+"F0.wireOp",EDGE,"E13.23.8"),sQuery(id+"F0.wireOp",EDGE,"E13.23.9"),sQuery(id+"F0.wireOp",EDGE,"E13.23.10"),sQuery(id+"F0.wireOp",EDGE,"E13.23.11"),sQuery(id+"F0.wireOp",EDGE,"E13.24.0"),sQuery(id+"F0.wireOp",EDGE,"E13.24.1"),sQuery(id+"F0.wireOp",EDGE,"E13.24.2"),sQuery(id+"F0.wireOp",EDGE,"E13.24.3"),sQuery(id+"F0.wireOp",EDGE,"E13.24.4"),sQuery(id+"F0.wireOp",EDGE,"E13.24.5"),sQuery(id+"F0.wireOp",EDGE,"E13.24.6"),sQuery(id+"F0.wireOp",EDGE,"E13.24.7"),sQuery(id+"F0.wireOp",EDGE,"E13.24.8"),sQuery(id+"F0.wireOp",EDGE,"E13.24.9"),sQuery(id+"F0.wireOp",EDGE,"E13.24.10"),sQuery(id+"F0.wireOp",EDGE,"E13.24.11"),sQuery(id+"F0.wireOp",EDGE,"E13.25.0"),sQuery(id+"F0.wireOp",EDGE,"E13.25.1"),sQuery(id+"F0.wireOp",EDGE,"E13.25.2"),sQuery(id+"F0.wireOp",EDGE,"E13.25.3"),sQuery(id+"F0.wireOp",EDGE,"E13.25.4"),sQuery(id+"F0.wireOp",EDGE,"E13.25.5"),sQuery(id+"F0.wireOp",EDGE,"E13.25.6"),sQuery(id+"F0.wireOp",EDGE,"E13.25.7"),sQuery(id+"F0.wireOp",EDGE,"E13.25.8"),sQuery(id+"F0.wireOp",EDGE,"E13.25.9"),sQuery(id+"F0.wireOp",EDGE,"E13.25.10"),sQuery(id+"F0.wireOp",EDGE,"E13.25.11"),sQuery(id+"F0.wireOp",EDGE,"E13.26.0"),sQuery(id+"F0.wireOp",EDGE,"E13.26.1"),sQuery(id+"F0.wireOp",EDGE,"E13.26.2"),sQuery(id+"F0.wireOp",EDGE,"E13.26.3"),sQuery(id+"F0.wireOp",EDGE,"E13.26.4"),sQuery(id+"F0.wireOp",EDGE,"E13.26.5"),sQuery(id+"F0.wireOp",EDGE,"E13.26.6"),sQuery(id+"F0.wireOp",EDGE,"E13.26.7"),sQuery(id+"F0.wireOp",EDGE,"E13.26.8"),sQuery(id+"F0.wireOp",EDGE,"E13.26.9"),sQuery(id+"F0.wireOp",EDGE,"E13.26.10"),sQuery(id+"F0.wireOp",EDGE,"E13.26.11"),sQuery(id+"F0.wireOp",EDGE,"E13.27.0"),sQuery(id+"F0.wireOp",EDGE,"E13.27.1"),sQuery(id+"F0.wireOp",EDGE,"E13.27.2"),sQuery(id+"F0.wireOp",EDGE,"E13.27.3"),sQuery(id+"F0.wireOp",EDGE,"E13.27.4"),sQuery(id+"F0.wireOp",EDGE,"E13.27.5"),sQuery(id+"F0.wireOp",EDGE,"E13.27.6"),sQuery(id+"F0.wireOp",EDGE,"E13.27.7"),sQuery(id+"F0.wireOp",EDGE,"E13.27.8"),sQuery(id+"F0.wireOp",EDGE,"E13.27.9"),sQuery(id+"F0.wireOp",EDGE,"E13.27.10"),sQuery(id+"F0.wireOp",EDGE,"E13.27.11"),sQuery(id+"F0.wireOp",EDGE,"E13.28.0"),sQuery(id+"F0.wireOp",EDGE,"E13.28.1"),sQuery(id+"F0.wireOp",EDGE,"E13.28.2"),sQuery(id+"F0.wireOp",EDGE,"E13.28.3"),sQuery(id+"F0.wireOp",EDGE,"E13.28.4"),sQuery(id+"F0.wireOp",EDGE,"E13.28.5"),sQuery(id+"F0.wireOp",EDGE,"E13.28.6"),sQuery(id+"F0.wireOp",EDGE,"E13.28.7"),sQuery(id+"F0.wireOp",EDGE,"E13.28.8"),sQuery(id+"F0.wireOp",EDGE,"E13.28.9"),sQuery(id+"F0.wireOp",EDGE,"E13.28.10"),sQuery(id+"F0.wireOp",EDGE,"E13.28.11"),sQuery(id+"F0.wireOp",EDGE,"E13.29.0"),sQuery(id+"F0.wireOp",EDGE,"E13.29.1"),sQuery(id+"F0.wireOp",EDGE,"E13.29.2"),sQuery(id+"F0.wireOp",EDGE,"E13.29.3"),sQuery(id+"F0.wireOp",EDGE,"E13.29.4"),sQuery(id+"F0.wireOp",EDGE,"E13.29.5"),sQuery(id+"F0.wireOp",EDGE,"E13.29.6"),sQuery(id+"F0.wireOp",EDGE,"E13.29.7"),sQuery(id+"F0.wireOp",EDGE,"E13.29.8"),sQuery(id+"F0.wireOp",EDGE,"E13.29.9"),sQuery(id+"F0.wireOp",EDGE,"E13.29.10"),sQuery(id+"F0.wireOp",EDGE,"E13.29.11"),sQuery(id+"F0.wireOp",EDGE,"E13.30.0"),sQuery(id+"F0.wireOp",EDGE,"E13.30.1"),sQuery(id+"F0.wireOp",EDGE,"E13.30.2"),sQuery(id+"F0.wireOp",EDGE,"E13.30.3"),sQuery(id+"F0.wireOp",EDGE,"E13.30.4"),sQuery(id+"F0.wireOp",EDGE,"E13.30.5"),sQuery(id+"F0.wireOp",EDGE,"E13.30.6"),sQuery(id+"F0.wireOp",EDGE,"E13.30.7"),sQuery(id+"F0.wireOp",EDGE,"E13.30.8"),sQuery(id+"F0.wireOp",EDGE,"E13.30.9"),sQuery(id+"F0.wireOp",EDGE,"E13.30.10"),sQuery(id+"F0.wireOp",EDGE,"E13.30.11"),sQuery(id+"F0.wireOp",EDGE,"E13.31.0"),sQuery(id+"F0.wireOp",EDGE,"E13.31.1"),sQuery(id+"F0.wireOp",EDGE,"E13.31.2"),sQuery(id+"F0.wireOp",EDGE,"E13.31.3"),sQuery(id+"F0.wireOp",EDGE,"E13.31.4"),sQuery(id+"F0.wireOp",EDGE,"E13.31.5"),sQuery(id+"F0.wireOp",EDGE,"E13.31.6"),sQuery(id+"F0.wireOp",EDGE,"E13.31.7"),sQuery(id+"F0.wireOp",EDGE,"E13.31.8"),sQuery(id+"F0.wireOp",EDGE,"E13.31.9"),sQuery(id+"F0.wireOp",EDGE,"E13.31.10"),sQuery(id+"F0.wireOp",EDGE,"E13.31.11"),sQuery(id+"F0.wireOp",EDGE,"E13.32.0"),sQuery(id+"F0.wireOp",EDGE,"E13.32.1"),sQuery(id+"F0.wireOp",EDGE,"E13.32.2"),sQuery(id+"F0.wireOp",EDGE,"E13.32.3"),sQuery(id+"F0.wireOp",EDGE,"E13.32.4"),sQuery(id+"F0.wireOp",EDGE,"E13.32.5"),sQuery(id+"F0.wireOp",EDGE,"E13.32.6"),sQuery(id+"F0.wireOp",EDGE,"E13.32.7"),sQuery(id+"F0.wireOp",EDGE,"E13.32.8"),sQuery(id+"F0.wireOp",EDGE,"E13.32.9"),sQuery(id+"F0.wireOp",EDGE,"E13.32.10"),sQuery(id+"F0.wireOp",EDGE,"E13.32.11"),sQuery(id+"F0.wireOp",EDGE,"E13.33.0"),sQuery(id+"F0.wireOp",EDGE,"E13.33.1"),sQuery(id+"F0.wireOp",EDGE,"E13.33.2"),sQuery(id+"F0.wireOp",EDGE,"E13.33.3"),sQuery(id+"F0.wireOp",EDGE,"E13.33.4"),sQuery(id+"F0.wireOp",EDGE,"E13.33.5"),sQuery(id+"F0.wireOp",EDGE,"E13.33.6"),sQuery(id+"F0.wireOp",EDGE,"E13.33.7"),sQuery(id+"F0.wireOp",EDGE,"E13.33.8"),sQuery(id+"F0.wireOp",EDGE,"E13.33.9"),sQuery(id+"F0.wireOp",EDGE,"E13.33.10"),sQuery(id+"F0.wireOp",EDGE,"E13.33.11"),sQuery(id+"F0.wireOp",EDGE,"E13.34.0"),sQuery(id+"F0.wireOp",EDGE,"E13.34.1"),sQuery(id+"F0.wireOp",EDGE,"E13.34.2"),sQuery(id+"F0.wireOp",EDGE,"E13.34.3"),sQuery(id+"F0.wireOp",EDGE,"E13.34.4"),sQuery(id+"F0.wireOp",EDGE,"E13.34.5"),sQuery(id+"F0.wireOp",EDGE,"E13.34.6"),sQuery(id+"F0.wireOp",EDGE,"E13.34.7"),sQuery(id+"F0.wireOp",EDGE,"E13.34.8"),sQuery(id+"F0.wireOp",EDGE,"E13.34.9"),sQuery(id+"F0.wireOp",EDGE,"E13.34.10"),sQuery(id+"F0.wireOp",EDGE,"E13.34.11"),sQuery(id+"F0.wireOp",EDGE,"E13.35.0"),sQuery(id+"F0.wireOp",EDGE,"E13.35.1"),sQuery(id+"F0.wireOp",EDGE,"E13.35.2"),sQuery(id+"F0.wireOp",EDGE,"E13.35.3"),sQuery(id+"F0.wireOp",EDGE,"E13.35.4"),sQuery(id+"F0.wireOp",EDGE,"E13.35.5"),sQuery(id+"F0.wireOp",EDGE,"E13.35.6"),sQuery(id+"F0.wireOp",EDGE,"E13.35.7"),sQuery(id+"F0.wireOp",EDGE,"E13.35.8"),sQuery(id+"F0.wireOp",EDGE,"E13.35.9"),sQuery(id+"F0.wireOp",EDGE,"E13.35.10"),sQuery(id+"F0.wireOp",EDGE,"E13.35.11"),sQuery(id+"F0.wireOp",EDGE,"E14.trimOffspring"),sQuery(id+"F0.wireOp",EDGE,"E15.trimOffspring"),sQuery(id+"F0.wireOp",EDGE,"E16.trimOffspring"),sQuery(id+"F0.wireOp",EDGE,"E17.trimOffspring"),sQuery(id+"F0.wireOp",EDGE,"E18.trimOffspring"),sQuery(id+"F0.wireOp",EDGE,"E19.trimOffspring"),sQuery(id+"F0.wireOp",EDGE,"E20.trimOffspring"),sQuery(id+"F0.wireOp",EDGE,"E21.trimOffspring"),sQuery(id+"F0.wireOp",EDGE,"E22.trimOffspring"),sQuery(id+"F0.wireOp",EDGE,"E23.trimOffspring"),sQuery(id+"F0.wireOp",EDGE,"E24.trimOffspring"),sQuery(id+"F0.wireOp",EDGE,"E25.trimOffspring"),sQuery(id+"F0.wireOp",EDGE,"E26.trimOffspring"),sQuery(id+"F0.wireOp",EDGE,"E27.trimOffspring"),sQuery(id+"F0.wireOp",EDGE,"E28.trimOffspring"),sQuery(id+"F0.wireOp",EDGE,"E29.trimOffspring"),sQuery(id+"F0.wireOp",EDGE,"E30.trimOffspring"),sQuery(id+"F0.wireOp",EDGE,"E31.trimOffspring"),sQuery(id+"F0.wireOp",EDGE,"E32.trimOffspring"),sQuery(id+"F0.wireOp",EDGE,"E33.trimOffspring"),sQuery(id+"F0.wireOp",EDGE,"E34.trimOffspring"),sQuery(id+"F0.wireOp",EDGE,"E35.trimOffspring"),sQuery(id+"F0.wireOp",EDGE,"E36.trimOffspring"),sQuery(id+"F0.wireOp",EDGE,"E37.trimOffspring"),sQuery(id+"F0.wireOp",EDGE,"E38.trimOffspring"),sQuery(id+"F0.wireOp",EDGE,"E39.trimOffspring"),sQuery(id+"F0.wireOp",EDGE,"E40.trimOffspring"),sQuery(id+"F0.wireOp",EDGE,"E41.trimOffspring"),sQuery(id+"F0.wireOp",EDGE,"E42.trimOffspring"),sQuery(id+"F0.wireOp",EDGE,"E43.trimOffspring"),sQuery(id+"F0.wireOp",EDGE,"E44.trimOffspring"),sQuery(id+"F0.wireOp",EDGE,"E45.trimOffspring"),sQuery(id+"F0.wireOp",EDGE,"E46.trimOffspring"),sQuery(id+"F0.wireOp",EDGE,"E47.trimOffspring"),sQuery(id+"F0.wireOp",EDGE,"E48.trimOffspring")])],"isStart":false});
            var sketch = newSketch(context, id + "F2", { "sketchPlane" : qUnion([Q0])});
            skCircle(sketch, "E49", {"center": v(0, 0) * mm, "radius": 3.18 * mm});
            skSolve(sketch);
        }
        {
            var Q0;
            Q0 = qSketchRegion(id + "F2", true);
            extrude(context, id + "F3", {"entities" : qUnion([Q0]), "operationType" : NewBodyOperationType.REMOVE, "endBound" : BoundingType.THROUGH_ALL, "oppositeDirection" : true, "depth" : 25.4 * mm});
        }
        {
            var Q0;
            Q0=makeQuery(id+"F1.opExtrude","CAP_FACE",FACE,{"disambiguationData":[OSD([sQuery(id+"F0.wireOp",EDGE,"E0"),sQuery(id+"F0.wireOp",EDGE,"E1"),sQuery(id+"F0.wireOp",EDGE,"E2"),sQuery(id+"F0.wireOp",EDGE,"E3"),sQuery(id+"F0.wireOp",EDGE,"E4.MirrorCS"),sQuery(id+"F0.wireOp",EDGE,"E5.MirrorCS"),sQuery(id+"F0.wireOp",EDGE,"E6.MirrorCS"),sQuery(id+"F0.wireOp",EDGE,"E7.filletArc"),sQuery(id+"F0.wireOp",EDGE,"E8.filletArc"),sQuery(id+"F0.wireOp",EDGE,"E9.filletArc"),sQuery(id+"F0.wireOp",EDGE,"E10.filletArc"),sQuery(id+"F0.wireOp",EDGE,"E11.filletArc"),sQuery(id+"F0.wireOp",EDGE,"E12.filletArc"),sQuery(id+"F0.wireOp",EDGE,"E13.1.0"),sQuery(id+"F0.wireOp",EDGE,"E13.1.1"),sQuery(id+"F0.wireOp",EDGE,"E13.1.2"),sQuery(id+"F0.wireOp",EDGE,"E13.1.3"),sQuery(id+"F0.wireOp",EDGE,"E13.1.4"),sQuery(id+"F0.wireOp",EDGE,"E13.1.5"),sQuery(id+"F0.wireOp",EDGE,"E13.1.6"),sQuery(id+"F0.wireOp",EDGE,"E13.1.7"),sQuery(id+"F0.wireOp",EDGE,"E13.1.8"),sQuery(id+"F0.wireOp",EDGE,"E13.1.9"),sQuery(id+"F0.wireOp",EDGE,"E13.1.10"),sQuery(id+"F0.wireOp",EDGE,"E13.1.11"),sQuery(id+"F0.wireOp",EDGE,"E13.2.0"),sQuery(id+"F0.wireOp",EDGE,"E13.2.1"),sQuery(id+"F0.wireOp",EDGE,"E13.2.2"),sQuery(id+"F0.wireOp",EDGE,"E13.2.3"),sQuery(id+"F0.wireOp",EDGE,"E13.2.4"),sQuery(id+"F0.wireOp",EDGE,"E13.2.5"),sQuery(id+"F0.wireOp",EDGE,"E13.2.6"),sQuery(id+"F0.wireOp",EDGE,"E13.2.7"),sQuery(id+"F0.wireOp",EDGE,"E13.2.8"),sQuery(id+"F0.wireOp",EDGE,"E13.2.9"),sQuery(id+"F0.wireOp",EDGE,"E13.2.10"),sQuery(id+"F0.wireOp",EDGE,"E13.2.11"),sQuery(id+"F0.wireOp",EDGE,"E13.3.0"),sQuery(id+"F0.wireOp",EDGE,"E13.3.1"),sQuery(id+"F0.wireOp",EDGE,"E13.3.2"),sQuery(id+"F0.wireOp",EDGE,"E13.3.3"),sQuery(id+"F0.wireOp",EDGE,"E13.3.4"),sQuery(id+"F0.wireOp",EDGE,"E13.3.5"),sQuery(id+"F0.wireOp",EDGE,"E13.3.6"),sQuery(id+"F0.wireOp",EDGE,"E13.3.7"),sQuery(id+"F0.wireOp",EDGE,"E13.3.8"),sQuery(id+"F0.wireOp",EDGE,"E13.3.9"),sQuery(id+"F0.wireOp",EDGE,"E13.3.10"),sQuery(id+"F0.wireOp",EDGE,"E13.3.11"),sQuery(id+"F0.wireOp",EDGE,"E13.4.0"),sQuery(id+"F0.wireOp",EDGE,"E13.4.1"),sQuery(id+"F0.wireOp",EDGE,"E13.4.2"),sQuery(id+"F0.wireOp",EDGE,"E13.4.3"),sQuery(id+"F0.wireOp",EDGE,"E13.4.4"),sQuery(id+"F0.wireOp",EDGE,"E13.4.5"),sQuery(id+"F0.wireOp",EDGE,"E13.4.6"),sQuery(id+"F0.wireOp",EDGE,"E13.4.7"),sQuery(id+"F0.wireOp",EDGE,"E13.4.8"),sQuery(id+"F0.wireOp",EDGE,"E13.4.9"),sQuery(id+"F0.wireOp",EDGE,"E13.4.10"),sQuery(id+"F0.wireOp",EDGE,"E13.4.11"),sQuery(id+"F0.wireOp",EDGE,"E13.5.0"),sQuery(id+"F0.wireOp",EDGE,"E13.5.1"),sQuery(id+"F0.wireOp",EDGE,"E13.5.2"),sQuery(id+"F0.wireOp",EDGE,"E13.5.3"),sQuery(id+"F0.wireOp",EDGE,"E13.5.4"),sQuery(id+"F0.wireOp",EDGE,"E13.5.5"),sQuery(id+"F0.wireOp",EDGE,"E13.5.6"),sQuery(id+"F0.wireOp",EDGE,"E13.5.7"),sQuery(id+"F0.wireOp",EDGE,"E13.5.8"),sQuery(id+"F0.wireOp",EDGE,"E13.5.9"),sQuery(id+"F0.wireOp",EDGE,"E13.5.10"),sQuery(id+"F0.wireOp",EDGE,"E13.5.11"),sQuery(id+"F0.wireOp",EDGE,"E13.6.0"),sQuery(id+"F0.wireOp",EDGE,"E13.6.1"),sQuery(id+"F0.wireOp",EDGE,"E13.6.2"),sQuery(id+"F0.wireOp",EDGE,"E13.6.3"),sQuery(id+"F0.wireOp",EDGE,"E13.6.4"),sQuery(id+"F0.wireOp",EDGE,"E13.6.5"),sQuery(id+"F0.wireOp",EDGE,"E13.6.6"),sQuery(id+"F0.wireOp",EDGE,"E13.6.7"),sQuery(id+"F0.wireOp",EDGE,"E13.6.8"),sQuery(id+"F0.wireOp",EDGE,"E13.6.9"),sQuery(id+"F0.wireOp",EDGE,"E13.6.10"),sQuery(id+"F0.wireOp",EDGE,"E13.6.11"),sQuery(id+"F0.wireOp",EDGE,"E13.7.0"),sQuery(id+"F0.wireOp",EDGE,"E13.7.1"),sQuery(id+"F0.wireOp",EDGE,"E13.7.2"),sQuery(id+"F0.wireOp",EDGE,"E13.7.3"),sQuery(id+"F0.wireOp",EDGE,"E13.7.4"),sQuery(id+"F0.wireOp",EDGE,"E13.7.5"),sQuery(id+"F0.wireOp",EDGE,"E13.7.6"),sQuery(id+"F0.wireOp",EDGE,"E13.7.7"),sQuery(id+"F0.wireOp",EDGE,"E13.7.8"),sQuery(id+"F0.wireOp",EDGE,"E13.7.9"),sQuery(id+"F0.wireOp",EDGE,"E13.7.10"),sQuery(id+"F0.wireOp",EDGE,"E13.7.11"),sQuery(id+"F0.wireOp",EDGE,"E13.8.0"),sQuery(id+"F0.wireOp",EDGE,"E13.8.1"),sQuery(id+"F0.wireOp",EDGE,"E13.8.2"),sQuery(id+"F0.wireOp",EDGE,"E13.8.3"),sQuery(id+"F0.wireOp",EDGE,"E13.8.4"),sQuery(id+"F0.wireOp",EDGE,"E13.8.5"),sQuery(id+"F0.wireOp",EDGE,"E13.8.6"),sQuery(id+"F0.wireOp",EDGE,"E13.8.7"),sQuery(id+"F0.wireOp",EDGE,"E13.8.8"),sQuery(id+"F0.wireOp",EDGE,"E13.8.9"),sQuery(id+"F0.wireOp",EDGE,"E13.8.10"),sQuery(id+"F0.wireOp",EDGE,"E13.8.11"),sQuery(id+"F0.wireOp",EDGE,"E13.9.0"),sQuery(id+"F0.wireOp",EDGE,"E13.9.1"),sQuery(id+"F0.wireOp",EDGE,"E13.9.2"),sQuery(id+"F0.wireOp",EDGE,"E13.9.3"),sQuery(id+"F0.wireOp",EDGE,"E13.9.4"),sQuery(id+"F0.wireOp",EDGE,"E13.9.5"),sQuery(id+"F0.wireOp",EDGE,"E13.9.6"),sQuery(id+"F0.wireOp",EDGE,"E13.9.7"),sQuery(id+"F0.wireOp",EDGE,"E13.9.8"),sQuery(id+"F0.wireOp",EDGE,"E13.9.9"),sQuery(id+"F0.wireOp",EDGE,"E13.9.10"),sQuery(id+"F0.wireOp",EDGE,"E13.9.11"),sQuery(id+"F0.wireOp",EDGE,"E13.10.0"),sQuery(id+"F0.wireOp",EDGE,"E13.10.1"),sQuery(id+"F0.wireOp",EDGE,"E13.10.2"),sQuery(id+"F0.wireOp",EDGE,"E13.10.3"),sQuery(id+"F0.wireOp",EDGE,"E13.10.4"),sQuery(id+"F0.wireOp",EDGE,"E13.10.5"),sQuery(id+"F0.wireOp",EDGE,"E13.10.6"),sQuery(id+"F0.wireOp",EDGE,"E13.10.7"),sQuery(id+"F0.wireOp",EDGE,"E13.10.8"),sQuery(id+"F0.wireOp",EDGE,"E13.10.9"),sQuery(id+"F0.wireOp",EDGE,"E13.10.10"),sQuery(id+"F0.wireOp",EDGE,"E13.10.11"),sQuery(id+"F0.wireOp",EDGE,"E13.11.0"),sQuery(id+"F0.wireOp",EDGE,"E13.11.1"),sQuery(id+"F0.wireOp",EDGE,"E13.11.2"),sQuery(id+"F0.wireOp",EDGE,"E13.11.3"),sQuery(id+"F0.wireOp",EDGE,"E13.11.4"),sQuery(id+"F0.wireOp",EDGE,"E13.11.5"),sQuery(id+"F0.wireOp",EDGE,"E13.11.6"),sQuery(id+"F0.wireOp",EDGE,"E13.11.7"),sQuery(id+"F0.wireOp",EDGE,"E13.11.8"),sQuery(id+"F0.wireOp",EDGE,"E13.11.9"),sQuery(id+"F0.wireOp",EDGE,"E13.11.10"),sQuery(id+"F0.wireOp",EDGE,"E13.11.11"),sQuery(id+"F0.wireOp",EDGE,"E13.12.0"),sQuery(id+"F0.wireOp",EDGE,"E13.12.1"),sQuery(id+"F0.wireOp",EDGE,"E13.12.2"),sQuery(id+"F0.wireOp",EDGE,"E13.12.3"),sQuery(id+"F0.wireOp",EDGE,"E13.12.4"),sQuery(id+"F0.wireOp",EDGE,"E13.12.5"),sQuery(id+"F0.wireOp",EDGE,"E13.12.6"),sQuery(id+"F0.wireOp",EDGE,"E13.12.7"),sQuery(id+"F0.wireOp",EDGE,"E13.12.8"),sQuery(id+"F0.wireOp",EDGE,"E13.12.9"),sQuery(id+"F0.wireOp",EDGE,"E13.12.10"),sQuery(id+"F0.wireOp",EDGE,"E13.12.11"),sQuery(id+"F0.wireOp",EDGE,"E13.13.0"),sQuery(id+"F0.wireOp",EDGE,"E13.13.1"),sQuery(id+"F0.wireOp",EDGE,"E13.13.2"),sQuery(id+"F0.wireOp",EDGE,"E13.13.3"),sQuery(id+"F0.wireOp",EDGE,"E13.13.4"),sQuery(id+"F0.wireOp",EDGE,"E13.13.5"),sQuery(id+"F0.wireOp",EDGE,"E13.13.6"),sQuery(id+"F0.wireOp",EDGE,"E13.13.7"),sQuery(id+"F0.wireOp",EDGE,"E13.13.8"),sQuery(id+"F0.wireOp",EDGE,"E13.13.9"),sQuery(id+"F0.wireOp",EDGE,"E13.13.10"),sQuery(id+"F0.wireOp",EDGE,"E13.13.11"),sQuery(id+"F0.wireOp",EDGE,"E13.14.0"),sQuery(id+"F0.wireOp",EDGE,"E13.14.1"),sQuery(id+"F0.wireOp",EDGE,"E13.14.2"),sQuery(id+"F0.wireOp",EDGE,"E13.14.3"),sQuery(id+"F0.wireOp",EDGE,"E13.14.4"),sQuery(id+"F0.wireOp",EDGE,"E13.14.5"),sQuery(id+"F0.wireOp",EDGE,"E13.14.6"),sQuery(id+"F0.wireOp",EDGE,"E13.14.7"),sQuery(id+"F0.wireOp",EDGE,"E13.14.8"),sQuery(id+"F0.wireOp",EDGE,"E13.14.9"),sQuery(id+"F0.wireOp",EDGE,"E13.14.10"),sQuery(id+"F0.wireOp",EDGE,"E13.14.11"),sQuery(id+"F0.wireOp",EDGE,"E13.15.0"),sQuery(id+"F0.wireOp",EDGE,"E13.15.1"),sQuery(id+"F0.wireOp",EDGE,"E13.15.2"),sQuery(id+"F0.wireOp",EDGE,"E13.15.3"),sQuery(id+"F0.wireOp",EDGE,"E13.15.4"),sQuery(id+"F0.wireOp",EDGE,"E13.15.5"),sQuery(id+"F0.wireOp",EDGE,"E13.15.6"),sQuery(id+"F0.wireOp",EDGE,"E13.15.7"),sQuery(id+"F0.wireOp",EDGE,"E13.15.8"),sQuery(id+"F0.wireOp",EDGE,"E13.15.9"),sQuery(id+"F0.wireOp",EDGE,"E13.15.10"),sQuery(id+"F0.wireOp",EDGE,"E13.15.11"),sQuery(id+"F0.wireOp",EDGE,"E13.16.0"),sQuery(id+"F0.wireOp",EDGE,"E13.16.1"),sQuery(id+"F0.wireOp",EDGE,"E13.16.2"),sQuery(id+"F0.wireOp",EDGE,"E13.16.3"),sQuery(id+"F0.wireOp",EDGE,"E13.16.4"),sQuery(id+"F0.wireOp",EDGE,"E13.16.5"),sQuery(id+"F0.wireOp",EDGE,"E13.16.6"),sQuery(id+"F0.wireOp",EDGE,"E13.16.7"),sQuery(id+"F0.wireOp",EDGE,"E13.16.8"),sQuery(id+"F0.wireOp",EDGE,"E13.16.9"),sQuery(id+"F0.wireOp",EDGE,"E13.16.10"),sQuery(id+"F0.wireOp",EDGE,"E13.16.11"),sQuery(id+"F0.wireOp",EDGE,"E13.17.0"),sQuery(id+"F0.wireOp",EDGE,"E13.17.1"),sQuery(id+"F0.wireOp",EDGE,"E13.17.2"),sQuery(id+"F0.wireOp",EDGE,"E13.17.3"),sQuery(id+"F0.wireOp",EDGE,"E13.17.4"),sQuery(id+"F0.wireOp",EDGE,"E13.17.5"),sQuery(id+"F0.wireOp",EDGE,"E13.17.6"),sQuery(id+"F0.wireOp",EDGE,"E13.17.7"),sQuery(id+"F0.wireOp",EDGE,"E13.17.8"),sQuery(id+"F0.wireOp",EDGE,"E13.17.9"),sQuery(id+"F0.wireOp",EDGE,"E13.17.10"),sQuery(id+"F0.wireOp",EDGE,"E13.17.11"),sQuery(id+"F0.wireOp",EDGE,"E13.18.0"),sQuery(id+"F0.wireOp",EDGE,"E13.18.1"),sQuery(id+"F0.wireOp",EDGE,"E13.18.2"),sQuery(id+"F0.wireOp",EDGE,"E13.18.3"),sQuery(id+"F0.wireOp",EDGE,"E13.18.4"),sQuery(id+"F0.wireOp",EDGE,"E13.18.5"),sQuery(id+"F0.wireOp",EDGE,"E13.18.6"),sQuery(id+"F0.wireOp",EDGE,"E13.18.7"),sQuery(id+"F0.wireOp",EDGE,"E13.18.8"),sQuery(id+"F0.wireOp",EDGE,"E13.18.9"),sQuery(id+"F0.wireOp",EDGE,"E13.18.10"),sQuery(id+"F0.wireOp",EDGE,"E13.18.11"),sQuery(id+"F0.wireOp",EDGE,"E13.19.0"),sQuery(id+"F0.wireOp",EDGE,"E13.19.1"),sQuery(id+"F0.wireOp",EDGE,"E13.19.2"),sQuery(id+"F0.wireOp",EDGE,"E13.19.3"),sQuery(id+"F0.wireOp",EDGE,"E13.19.4"),sQuery(id+"F0.wireOp",EDGE,"E13.19.5"),sQuery(id+"F0.wireOp",EDGE,"E13.19.6"),sQuery(id+"F0.wireOp",EDGE,"E13.19.7"),sQuery(id+"F0.wireOp",EDGE,"E13.19.8"),sQuery(id+"F0.wireOp",EDGE,"E13.19.9"),sQuery(id+"F0.wireOp",EDGE,"E13.19.10"),sQuery(id+"F0.wireOp",EDGE,"E13.19.11"),sQuery(id+"F0.wireOp",EDGE,"E13.20.0"),sQuery(id+"F0.wireOp",EDGE,"E13.20.1"),sQuery(id+"F0.wireOp",EDGE,"E13.20.2"),sQuery(id+"F0.wireOp",EDGE,"E13.20.3"),sQuery(id+"F0.wireOp",EDGE,"E13.20.4"),sQuery(id+"F0.wireOp",EDGE,"E13.20.5"),sQuery(id+"F0.wireOp",EDGE,"E13.20.6"),sQuery(id+"F0.wireOp",EDGE,"E13.20.7"),sQuery(id+"F0.wireOp",EDGE,"E13.20.8"),sQuery(id+"F0.wireOp",EDGE,"E13.20.9"),sQuery(id+"F0.wireOp",EDGE,"E13.20.10"),sQuery(id+"F0.wireOp",EDGE,"E13.20.11"),sQuery(id+"F0.wireOp",EDGE,"E13.21.0"),sQuery(id+"F0.wireOp",EDGE,"E13.21.1"),sQuery(id+"F0.wireOp",EDGE,"E13.21.2"),sQuery(id+"F0.wireOp",EDGE,"E13.21.3"),sQuery(id+"F0.wireOp",EDGE,"E13.21.4"),sQuery(id+"F0.wireOp",EDGE,"E13.21.5"),sQuery(id+"F0.wireOp",EDGE,"E13.21.6"),sQuery(id+"F0.wireOp",EDGE,"E13.21.7"),sQuery(id+"F0.wireOp",EDGE,"E13.21.8"),sQuery(id+"F0.wireOp",EDGE,"E13.21.9"),sQuery(id+"F0.wireOp",EDGE,"E13.21.10"),sQuery(id+"F0.wireOp",EDGE,"E13.21.11"),sQuery(id+"F0.wireOp",EDGE,"E13.22.0"),sQuery(id+"F0.wireOp",EDGE,"E13.22.1"),sQuery(id+"F0.wireOp",EDGE,"E13.22.2"),sQuery(id+"F0.wireOp",EDGE,"E13.22.3"),sQuery(id+"F0.wireOp",EDGE,"E13.22.4"),sQuery(id+"F0.wireOp",EDGE,"E13.22.5"),sQuery(id+"F0.wireOp",EDGE,"E13.22.6"),sQuery(id+"F0.wireOp",EDGE,"E13.22.7"),sQuery(id+"F0.wireOp",EDGE,"E13.22.8"),sQuery(id+"F0.wireOp",EDGE,"E13.22.9"),sQuery(id+"F0.wireOp",EDGE,"E13.22.10"),sQuery(id+"F0.wireOp",EDGE,"E13.22.11"),sQuery(id+"F0.wireOp",EDGE,"E13.23.0"),sQuery(id+"F0.wireOp",EDGE,"E13.23.1"),sQuery(id+"F0.wireOp",EDGE,"E13.23.2"),sQuery(id+"F0.wireOp",EDGE,"E13.23.3"),sQuery(id+"F0.wireOp",EDGE,"E13.23.4"),sQuery(id+"F0.wireOp",EDGE,"E13.23.5"),sQuery(id+"F0.wireOp",EDGE,"E13.23.6"),sQuery(id+"F0.wireOp",EDGE,"E13.23.7"),sQuery(id+"F0.wireOp",EDGE,"E13.23.8"),sQuery(id+"F0.wireOp",EDGE,"E13.23.9"),sQuery(id+"F0.wireOp",EDGE,"E13.23.10"),sQuery(id+"F0.wireOp",EDGE,"E13.23.11"),sQuery(id+"F0.wireOp",EDGE,"E13.24.0"),sQuery(id+"F0.wireOp",EDGE,"E13.24.1"),sQuery(id+"F0.wireOp",EDGE,"E13.24.2"),sQuery(id+"F0.wireOp",EDGE,"E13.24.3"),sQuery(id+"F0.wireOp",EDGE,"E13.24.4"),sQuery(id+"F0.wireOp",EDGE,"E13.24.5"),sQuery(id+"F0.wireOp",EDGE,"E13.24.6"),sQuery(id+"F0.wireOp",EDGE,"E13.24.7"),sQuery(id+"F0.wireOp",EDGE,"E13.24.8"),sQuery(id+"F0.wireOp",EDGE,"E13.24.9"),sQuery(id+"F0.wireOp",EDGE,"E13.24.10"),sQuery(id+"F0.wireOp",EDGE,"E13.24.11"),sQuery(id+"F0.wireOp",EDGE,"E13.25.0"),sQuery(id+"F0.wireOp",EDGE,"E13.25.1"),sQuery(id+"F0.wireOp",EDGE,"E13.25.2"),sQuery(id+"F0.wireOp",EDGE,"E13.25.3"),sQuery(id+"F0.wireOp",EDGE,"E13.25.4"),sQuery(id+"F0.wireOp",EDGE,"E13.25.5"),sQuery(id+"F0.wireOp",EDGE,"E13.25.6"),sQuery(id+"F0.wireOp",EDGE,"E13.25.7"),sQuery(id+"F0.wireOp",EDGE,"E13.25.8"),sQuery(id+"F0.wireOp",EDGE,"E13.25.9"),sQuery(id+"F0.wireOp",EDGE,"E13.25.10"),sQuery(id+"F0.wireOp",EDGE,"E13.25.11"),sQuery(id+"F0.wireOp",EDGE,"E13.26.0"),sQuery(id+"F0.wireOp",EDGE,"E13.26.1"),sQuery(id+"F0.wireOp",EDGE,"E13.26.2"),sQuery(id+"F0.wireOp",EDGE,"E13.26.3"),sQuery(id+"F0.wireOp",EDGE,"E13.26.4"),sQuery(id+"F0.wireOp",EDGE,"E13.26.5"),sQuery(id+"F0.wireOp",EDGE,"E13.26.6"),sQuery(id+"F0.wireOp",EDGE,"E13.26.7"),sQuery(id+"F0.wireOp",EDGE,"E13.26.8"),sQuery(id+"F0.wireOp",EDGE,"E13.26.9"),sQuery(id+"F0.wireOp",EDGE,"E13.26.10"),sQuery(id+"F0.wireOp",EDGE,"E13.26.11"),sQuery(id+"F0.wireOp",EDGE,"E13.27.0"),sQuery(id+"F0.wireOp",EDGE,"E13.27.1"),sQuery(id+"F0.wireOp",EDGE,"E13.27.2"),sQuery(id+"F0.wireOp",EDGE,"E13.27.3"),sQuery(id+"F0.wireOp",EDGE,"E13.27.4"),sQuery(id+"F0.wireOp",EDGE,"E13.27.5"),sQuery(id+"F0.wireOp",EDGE,"E13.27.6"),sQuery(id+"F0.wireOp",EDGE,"E13.27.7"),sQuery(id+"F0.wireOp",EDGE,"E13.27.8"),sQuery(id+"F0.wireOp",EDGE,"E13.27.9"),sQuery(id+"F0.wireOp",EDGE,"E13.27.10"),sQuery(id+"F0.wireOp",EDGE,"E13.27.11"),sQuery(id+"F0.wireOp",EDGE,"E13.28.0"),sQuery(id+"F0.wireOp",EDGE,"E13.28.1"),sQuery(id+"F0.wireOp",EDGE,"E13.28.2"),sQuery(id+"F0.wireOp",EDGE,"E13.28.3"),sQuery(id+"F0.wireOp",EDGE,"E13.28.4"),sQuery(id+"F0.wireOp",EDGE,"E13.28.5"),sQuery(id+"F0.wireOp",EDGE,"E13.28.6"),sQuery(id+"F0.wireOp",EDGE,"E13.28.7"),sQuery(id+"F0.wireOp",EDGE,"E13.28.8"),sQuery(id+"F0.wireOp",EDGE,"E13.28.9"),sQuery(id+"F0.wireOp",EDGE,"E13.28.10"),sQuery(id+"F0.wireOp",EDGE,"E13.28.11"),sQuery(id+"F0.wireOp",EDGE,"E13.29.0"),sQuery(id+"F0.wireOp",EDGE,"E13.29.1"),sQuery(id+"F0.wireOp",EDGE,"E13.29.2"),sQuery(id+"F0.wireOp",EDGE,"E13.29.3"),sQuery(id+"F0.wireOp",EDGE,"E13.29.4"),sQuery(id+"F0.wireOp",EDGE,"E13.29.5"),sQuery(id+"F0.wireOp",EDGE,"E13.29.6"),sQuery(id+"F0.wireOp",EDGE,"E13.29.7"),sQuery(id+"F0.wireOp",EDGE,"E13.29.8"),sQuery(id+"F0.wireOp",EDGE,"E13.29.9"),sQuery(id+"F0.wireOp",EDGE,"E13.29.10"),sQuery(id+"F0.wireOp",EDGE,"E13.29.11"),sQuery(id+"F0.wireOp",EDGE,"E13.30.0"),sQuery(id+"F0.wireOp",EDGE,"E13.30.1"),sQuery(id+"F0.wireOp",EDGE,"E13.30.2"),sQuery(id+"F0.wireOp",EDGE,"E13.30.3"),sQuery(id+"F0.wireOp",EDGE,"E13.30.4"),sQuery(id+"F0.wireOp",EDGE,"E13.30.5"),sQuery(id+"F0.wireOp",EDGE,"E13.30.6"),sQuery(id+"F0.wireOp",EDGE,"E13.30.7"),sQuery(id+"F0.wireOp",EDGE,"E13.30.8"),sQuery(id+"F0.wireOp",EDGE,"E13.30.9"),sQuery(id+"F0.wireOp",EDGE,"E13.30.10"),sQuery(id+"F0.wireOp",EDGE,"E13.30.11"),sQuery(id+"F0.wireOp",EDGE,"E13.31.0"),sQuery(id+"F0.wireOp",EDGE,"E13.31.1"),sQuery(id+"F0.wireOp",EDGE,"E13.31.2"),sQuery(id+"F0.wireOp",EDGE,"E13.31.3"),sQuery(id+"F0.wireOp",EDGE,"E13.31.4"),sQuery(id+"F0.wireOp",EDGE,"E13.31.5"),sQuery(id+"F0.wireOp",EDGE,"E13.31.6"),sQuery(id+"F0.wireOp",EDGE,"E13.31.7"),sQuery(id+"F0.wireOp",EDGE,"E13.31.8"),sQuery(id+"F0.wireOp",EDGE,"E13.31.9"),sQuery(id+"F0.wireOp",EDGE,"E13.31.10"),sQuery(id+"F0.wireOp",EDGE,"E13.31.11"),sQuery(id+"F0.wireOp",EDGE,"E13.32.0"),sQuery(id+"F0.wireOp",EDGE,"E13.32.1"),sQuery(id+"F0.wireOp",EDGE,"E13.32.2"),sQuery(id+"F0.wireOp",EDGE,"E13.32.3"),sQuery(id+"F0.wireOp",EDGE,"E13.32.4"),sQuery(id+"F0.wireOp",EDGE,"E13.32.5"),sQuery(id+"F0.wireOp",EDGE,"E13.32.6"),sQuery(id+"F0.wireOp",EDGE,"E13.32.7"),sQuery(id+"F0.wireOp",EDGE,"E13.32.8"),sQuery(id+"F0.wireOp",EDGE,"E13.32.9"),sQuery(id+"F0.wireOp",EDGE,"E13.32.10"),sQuery(id+"F0.wireOp",EDGE,"E13.32.11"),sQuery(id+"F0.wireOp",EDGE,"E13.33.0"),sQuery(id+"F0.wireOp",EDGE,"E13.33.1"),sQuery(id+"F0.wireOp",EDGE,"E13.33.2"),sQuery(id+"F0.wireOp",EDGE,"E13.33.3"),sQuery(id+"F0.wireOp",EDGE,"E13.33.4"),sQuery(id+"F0.wireOp",EDGE,"E13.33.5"),sQuery(id+"F0.wireOp",EDGE,"E13.33.6"),sQuery(id+"F0.wireOp",EDGE,"E13.33.7"),sQuery(id+"F0.wireOp",EDGE,"E13.33.8"),sQuery(id+"F0.wireOp",EDGE,"E13.33.9"),sQuery(id+"F0.wireOp",EDGE,"E13.33.10"),sQuery(id+"F0.wireOp",EDGE,"E13.33.11"),sQuery(id+"F0.wireOp",EDGE,"E13.34.0"),sQuery(id+"F0.wireOp",EDGE,"E13.34.1"),sQuery(id+"F0.wireOp",EDGE,"E13.34.2"),sQuery(id+"F0.wireOp",EDGE,"E13.34.3"),sQuery(id+"F0.wireOp",EDGE,"E13.34.4"),sQuery(id+"F0.wireOp",EDGE,"E13.34.5"),sQuery(id+"F0.wireOp",EDGE,"E13.34.6"),sQuery(id+"F0.wireOp",EDGE,"E13.34.7"),sQuery(id+"F0.wireOp",EDGE,"E13.34.8"),sQuery(id+"F0.wireOp",EDGE,"E13.34.9"),sQuery(id+"F0.wireOp",EDGE,"E13.34.10"),sQuery(id+"F0.wireOp",EDGE,"E13.34.11"),sQuery(id+"F0.wireOp",EDGE,"E13.35.0"),sQuery(id+"F0.wireOp",EDGE,"E13.35.1"),sQuery(id+"F0.wireOp",EDGE,"E13.35.2"),sQuery(id+"F0.wireOp",EDGE,"E13.35.3"),sQuery(id+"F0.wireOp",EDGE,"E13.35.4"),sQuery(id+"F0.wireOp",EDGE,"E13.35.5"),sQuery(id+"F0.wireOp",EDGE,"E13.35.6"),sQuery(id+"F0.wireOp",EDGE,"E13.35.7"),sQuery(id+"F0.wireOp",EDGE,"E13.35.8"),sQuery(id+"F0.wireOp",EDGE,"E13.35.9"),sQuery(id+"F0.wireOp",EDGE,"E13.35.10"),sQuery(id+"F0.wireOp",EDGE,"E13.35.11"),sQuery(id+"F0.wireOp",EDGE,"E14.trimOffspring"),sQuery(id+"F0.wireOp",EDGE,"E15.trimOffspring"),sQuery(id+"F0.wireOp",EDGE,"E16.trimOffspring"),sQuery(id+"F0.wireOp",EDGE,"E17.trimOffspring"),sQuery(id+"F0.wireOp",EDGE,"E18.trimOffspring"),sQuery(id+"F0.wireOp",EDGE,"E19.trimOffspring"),sQuery(id+"F0.wireOp",EDGE,"E20.trimOffspring"),sQuery(id+"F0.wireOp",EDGE,"E21.trimOffspring"),sQuery(id+"F0.wireOp",EDGE,"E22.trimOffspring"),sQuery(id+"F0.wireOp",EDGE,"E23.trimOffspring"),sQuery(id+"F0.wireOp",EDGE,"E24.trimOffspring"),sQuery(id+"F0.wireOp",EDGE,"E25.trimOffspring"),sQuery(id+"F0.wireOp",EDGE,"E26.trimOffspring"),sQuery(id+"F0.wireOp",EDGE,"E27.trimOffspring"),sQuery(id+"F0.wireOp",EDGE,"E28.trimOffspring"),sQuery(id+"F0.wireOp",EDGE,"E29.trimOffspring"),sQuery(id+"F0.wireOp",EDGE,"E30.trimOffspring"),sQuery(id+"F0.wireOp",EDGE,"E31.trimOffspring"),sQuery(id+"F0.wireOp",EDGE,"E32.trimOffspring"),sQuery(id+"F0.wireOp",EDGE,"E33.trimOffspring"),sQuery(id+"F0.wireOp",EDGE,"E34.trimOffspring"),sQuery(id+"F0.wireOp",EDGE,"E35.trimOffspring"),sQuery(id+"F0.wireOp",EDGE,"E36.trimOffspring"),sQuery(id+"F0.wireOp",EDGE,"E37.trimOffspring"),sQuery(id+"F0.wireOp",EDGE,"E38.trimOffspring"),sQuery(id+"F0.wireOp",EDGE,"E39.trimOffspring"),sQuery(id+"F0.wireOp",EDGE,"E40.trimOffspring"),sQuery(id+"F0.wireOp",EDGE,"E41.trimOffspring"),sQuery(id+"F0.wireOp",EDGE,"E42.trimOffspring"),sQuery(id+"F0.wireOp",EDGE,"E43.trimOffspring"),sQuery(id+"F0.wireOp",EDGE,"E44.trimOffspring"),sQuery(id+"F0.wireOp",EDGE,"E45.trimOffspring"),sQuery(id+"F0.wireOp",EDGE,"E46.trimOffspring"),sQuery(id+"F0.wireOp",EDGE,"E47.trimOffspring"),sQuery(id+"F0.wireOp",EDGE,"E48.trimOffspring")])],"isStart":false});
            shell(context, id + "F4", {"entities" : qUnion([Q0]), "thickness" : 6.35 * mm});
        }
        {
            var Q0;
            Q0=qCreatedBy(makeId("Right.planeOp"),FACE);
            cPlane(context, id + "F5", {"entities" : qUnion([Q0]), "cplaneType" : CPlaneType.OFFSET, "offset" : 9.52 * mm, "width" : 152.4 * mm, "height" : 152.4 * mm});
        }
        {
            var Q0;
            Q0=qCreatedBy(id+"F5.planeOp",FACE);
            var sketch = newSketch(context, id + "F6", { "sketchPlane" : qUnion([Q0])});
            skCircle(sketch, "E50", {"center": v(-8.4, -1.5) * mm, "radius": 1.13 * mm});
            skSolve(sketch);
        }
        {
            var Q0;
            Q0 = qSketchRegion(id + "F6", true);
            extrude(context, id + "F7", {"entities" : qUnion([Q0]), "operationType" : NewBodyOperationType.REMOVE, "oppositeDirection" : true, "depth" : 8.25 * mm});
        }
    });
